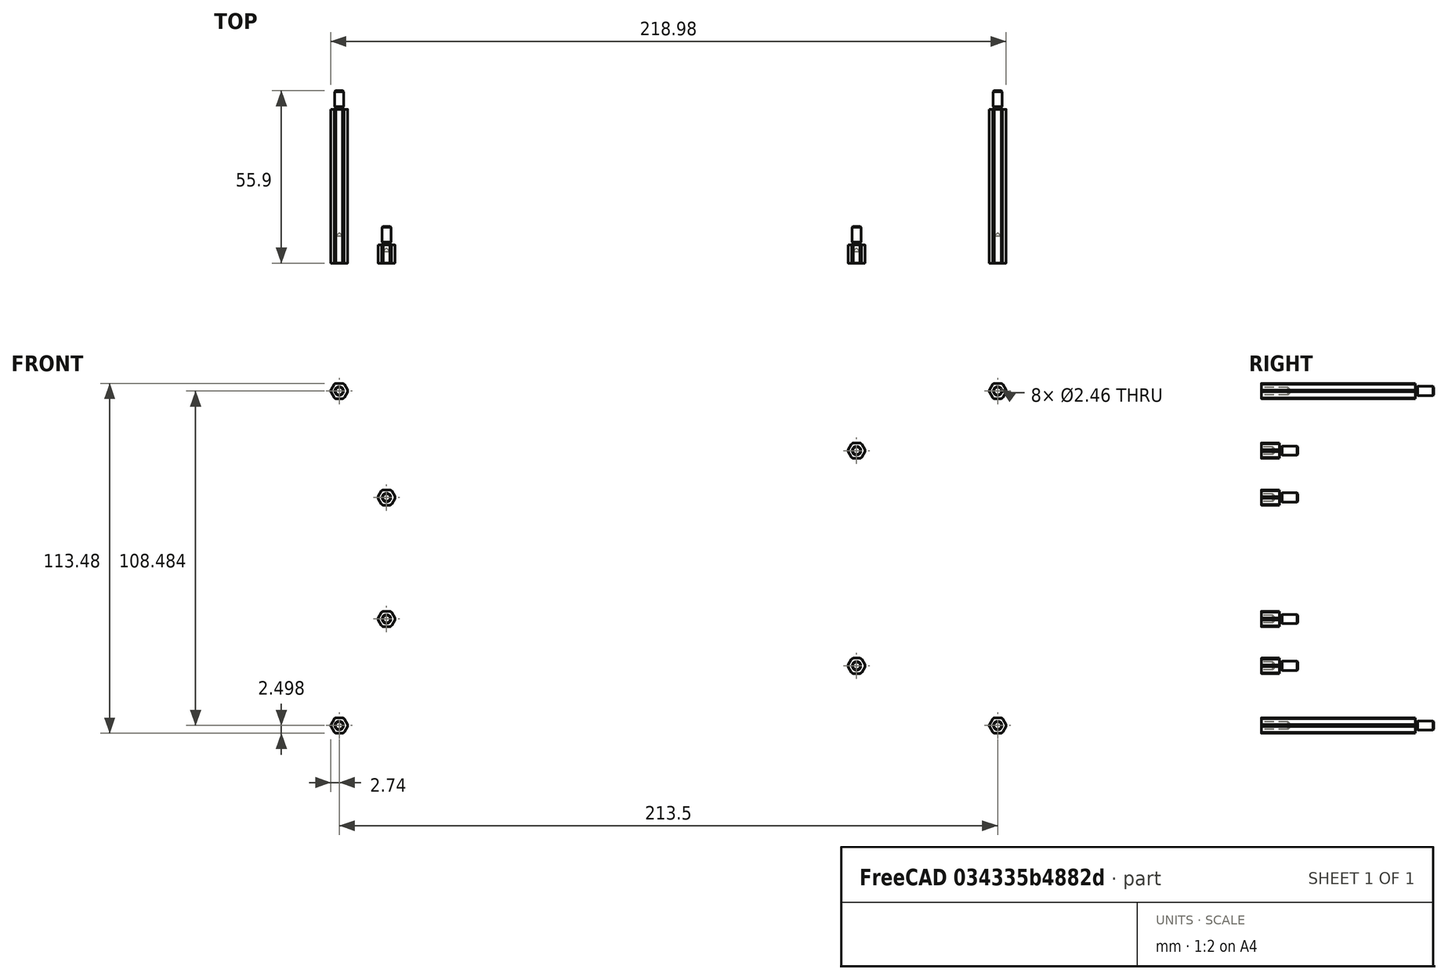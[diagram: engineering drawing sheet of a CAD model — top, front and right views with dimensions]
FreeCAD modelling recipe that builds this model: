
FCSTD DOCUMENT  (FreeCAD 1.0R38641 +468 (Git))
Label: psu
License: All rights reserved
LicenseURL: https://en.wikipedia.org/wiki/All_rights_reserved
objects: App::Link×8, App::FeaturePython×8, Part::FeaturePython×8, Assembly::JointGroup×1, Assembly::AssemblyObject×1
note: 8 computed .brp shape members not serialized (recipe doc carries the construction recipe); baked Part::Feature solids carry a one-line shape summary decoded from their .brp
EXTERNAL_REF file=parts/psu/psu_top_and_bottom.FCStd obj=Body
EXTERNAL_REF file=parts/psu/psu_side_short.FCStd obj=Body
EXTERNAL_REF file=parts/psu/psu_side_long.FCStd obj=Body
EXTERNAL_REF file=third_party/qualtek_power_entry.FCStd obj=Body
EXTERNAL_REF file=parts/dimensions.FCStd obj=VarSet
EXTERNAL_REF file=third_party/doepfer_psu3.FCStd obj=Body

FEATURE [App::Link] PsuTopAndBottom
  LinkedObject = -> <external parts/psu/psu_top_and_bottom.FCStd>#Body
FEATURE [App::FeaturePython] GroundedJoint  # Assembly grounded joint (typed FeaturePython)
  ObjectToGround = -> PsuTopAndBottom
FEATURE [App::Link] PsuTopAndBottom001
  LinkPlacement = pos=(-6e-15,-51.8542,-3e-16) rot=(0,0,1;0rad)
  LinkedObject = -> <external parts/psu/psu_top_and_bottom.FCStd>#Body
  Placement = pos=(-6e-15,-51.8542,-3e-16) rot=(0,0,1;0rad)
FEATURE [App::Link] PsuSideShort
  LinkPlacement = pos=(0.127,-51.8542,1.5e-14) rot=(0,0,1;0rad)
  LinkedObject = -> <external parts/psu/psu_side_short.FCStd>#Body
  Placement = pos=(0.127,-51.8542,1.5e-14) rot=(0,0,1;0rad)
FEATURE [App::Link] PsuSideShort001
  LinkPlacement = pos=(-227.198,-51.8542,1.832e-13) rot=(0,0,1;0rad)
  LinkedObject = -> <external parts/psu/psu_side_short.FCStd>#Body
  Placement = pos=(-227.198,-51.8542,1.832e-13) rot=(0,0,1;0rad)
FEATURE [App::Link] PsuSideLong
  LinkPlacement = pos=(2.22e-14,-51.8542,0.127) rot=(0,0,1;0rad)
  LinkedObject = -> <external parts/psu/psu_side_long.FCStd>#Body
  Placement = pos=(2.22e-14,-51.8542,0.127) rot=(0,0,1;0rad)
FEATURE [App::Link] PsuSideLong001
  LinkPlacement = pos=(2.26e-14,-51.8542,-86.1976) rot=(0,0,1;0rad)
  LinkedObject = -> <external parts/psu/psu_side_long.FCStd>#Body
  Placement = pos=(2.26e-14,-51.8542,-86.1976) rot=(0,0,1;0rad)
FEATURE [App::Link] PowerEntry
  LinkPlacement = pos=(333.089,127.227,-56.25) rot=(0,0.707107,-0.707107;3.14159rad)
  LinkedObject = -> <external third_party/qualtek_power_entry.FCStd>#Body
  Placement = pos=(333.089,127.227,-56.25) rot=(0,0.707107,-0.707107;3.14159rad)
FEATURE [App::FeaturePython] Joint  label="Fixed"  # Assembly joint (typed FeaturePython)
  Activated = true
  AngleMax = 0
  AngleMin = 0
  Detach1 = false
  Detach2 = false
  Distance = 0
  Distance2 = 0
  EnableAngleMax = false
  EnableAngleMin = false
  EnableLengthMax = false
  EnableLengthMin = false
  JointType = 0 (Fixed)
  LengthMax = 0
  LengthMin = 0
  Offset2 = pos=(0.127,0,0.127) rot=(0,0,1;0rad)
  Placement1 = pos=(328.216,127.227,-24.579) rot=(0,0,1;0rad)
  Placement2 = pos=(328.089,179.081,-24.579) rot=(0,0,1;0rad)
  Reference1 = -> Assembly [PsuTopAndBottom.Vertex91,PsuTopAndBottom.Vertex91]
  Reference2 = -> Assembly [PsuSideShort.Vertex42,PsuSideShort.Vertex42]
  expr: .Offset2.Base.x = dimensions#VarSet.EnclosureFinishThickness
  expr: .Offset2.Base.z = dimensions#VarSet.EnclosureFinishThickness
FEATURE [App::FeaturePython] Joint001  label="Fixed001"  # Assembly joint (typed FeaturePython)
  Activated = true
  AngleMax = 0
  AngleMin = 0
  Detach1 = false
  Detach2 = false
  Distance = 0
  Distance2 = 0
  EnableAngleMax = false
  EnableAngleMin = false
  EnableLengthMax = false
  EnableLengthMin = false
  JointType = 0 (Fixed)
  LengthMax = 0
  LengthMin = 0
  Offset1 = pos=(0.127,0,0.127) rot=(0,0,1;0rad)
  Placement1 = pos=(328.089,179.081,-24.579) rot=(0,0,1;0rad)
  Placement2 = pos=(100.892,127.227,-24.579) rot=(0,0,1;0rad)
  Reference1 = -> Assembly [PsuSideShort001.Vertex42,PsuSideShort001.Vertex42]
  Reference2 = -> Assembly [PsuTopAndBottom.Vertex67,PsuTopAndBottom.Vertex67]
  expr: .Offset1.Base.x = dimensions#VarSet.EnclosureFinishThickness
  expr: .Offset1.Base.z = dimensions#VarSet.EnclosureFinishThickness
FEATURE [App::FeaturePython] Joint002  label="Fixed002"  # Assembly joint (typed FeaturePython)
  Activated = true
  AngleMax = 0
  AngleMin = 0
  Detach1 = false
  Detach2 = false
  Distance = 0
  Distance2 = 0
  EnableAngleMax = false
  EnableAngleMin = false
  EnableLengthMax = false
  EnableLengthMin = false
  JointType = 0 (Fixed)
  LengthMax = 0
  LengthMin = 0
  Offset2 = pos=(0.127,0,0.127) rot=(0,0,1;0rad)
  Placement1 = pos=(328.216,127.227,-24.579) rot=(0,0,1;0rad)
  Placement2 = pos=(328.089,127.227,-24.579) rot=(0,0,1;0rad)
  Reference1 = -> Assembly [PsuTopAndBottom001.Vertex91,PsuTopAndBottom001.Vertex91]
  Reference2 = -> Assembly [PsuSideShort.Vertex10,PsuSideShort.Vertex10]
  expr: .Offset2.Base.x = dimensions#VarSet.EnclosureFinishThickness
  expr: .Offset2.Base.z = dimensions#VarSet.EnclosureFinishThickness
FEATURE [App::FeaturePython] Joint003  label="Fixed003"  # Assembly joint (typed FeaturePython)
  Activated = true
  AngleMax = 0
  AngleMin = 0
  Detach1 = false
  Detach2 = false
  Distance = 0
  Distance2 = 0
  EnableAngleMax = false
  EnableAngleMin = false
  EnableLengthMax = false
  EnableLengthMin = false
  JointType = 0 (Fixed)
  LengthMax = 0
  LengthMin = 0
  Offset1 = pos=(0.127,0,0.127) rot=(0,0,1;0rad)
  Placement1 = pos=(303.647,127.227,-12.1606) rot=(0,0,1;0rad)
  Placement2 = pos=(303.647,127.227,-12.0336) rot=(0,0,1;0rad)
  Reference1 = -> Assembly [PsuSideLong.Vertex28,PsuSideLong.Vertex28]
  Reference2 = -> Assembly [PsuTopAndBottom001.Vertex105,PsuTopAndBottom001.Vertex105]
  expr: .Offset1.Base.x = dimensions#VarSet.EnclosureFinishThickness
  expr: .Offset1.Base.z = dimensions#VarSet.EnclosureFinishThickness
FEATURE [App::FeaturePython] Joint004  label="Fixed004"  # Assembly joint (typed FeaturePython)
  Activated = true
  AngleMax = 0
  AngleMin = 0
  Detach1 = false
  Detach2 = false
  Distance = 0
  Distance2 = 0
  EnableAngleMax = false
  EnableAngleMin = false
  EnableLengthMax = false
  EnableLengthMin = false
  JointType = 0 (Fixed)
  LengthMax = 0
  LengthMin = 0
  Offset1 = pos=(-0.127,0,-0.127) rot=(0,0,1;0rad)
  Placement1 = pos=(303.52,127.227,-98.4852) rot=(0,0,1;0rad)
  Placement2 = pos=(303.52,127.227,-12.2876) rot=(0,0,1;0rad)
  Reference1 = -> Assembly [PsuTopAndBottom001.Vertex97,PsuTopAndBottom001.Vertex97]
  Reference2 = -> Assembly [PsuSideLong001.Vertex28,PsuSideLong001.Vertex28]
  expr: .Offset1.Base.x = -dimensions#VarSet.EnclosureFinishThickness
  expr: .Offset1.Base.z = -dimensions#VarSet.EnclosureFinishThickness
FEATURE [App::FeaturePython] Joint007  label="Fixed007"  # Assembly joint (typed FeaturePython)
  Activated = true
  AngleMax = 0
  AngleMin = 0
  Detach1 = false
  Detach2 = false
  Distance = 0
  Distance2 = 0
  EnableAngleMax = false
  EnableAngleMin = false
  EnableLengthMax = false
  EnableLengthMin = false
  JointType = 0 (Fixed)
  LengthMax = 0
  LengthMin = 0
  Offset2 = pos=(0,0,0) rot=(0,0,-1;1.5708rad)
  Placement1 = pos=(5,-7.1e-15,5) rot=(-0.57735,-0.57735,0.57735;2.0944rad)
  Placement2 = pos=(327.962,174.081,-56.25) rot=(0,1,0;1.5708rad)
  Reference1 = -> Assembly [PowerEntry.Edge36,PowerEntry.Edge36]
  Reference2 = -> Assembly [PsuSideShort.Edge123,PsuSideShort.Edge123]
FEATURE [Part::FeaturePython] Standoff  label="M3x6x5-Standoff"  # WARN: FeaturePython — macro-defined, semantics opaque (R4)
  BaseObject = -> PsuTopAndBottom001 [Pad.Edge183]
  Diameter = 2
  Invert = true
  LeftHanded = false
  Length = 4
  LengthCustom = 6
  MatchOuter = false
  Offset = -6
  OffsetAngle = 0
  Placement = pos=(274.5,83.2271,-21.35) rot=(1,0,0;1.5708rad)
  ScrewLength = 6
  Thread = false
  Type = 0
  Width = 0
FEATURE [Part::FeaturePython] Standoff001  label="M3x6x5-Standoff019"  # WARN: FeaturePython — macro-defined, semantics opaque (R4)
  BaseObject = -> PsuTopAndBottom001 [Pad.Edge186]
  Diameter = 2
  Invert = true
  LeftHanded = false
  Length = 4
  LengthCustom = 6
  MatchOuter = false
  Offset = -6
  OffsetAngle = 0
  Placement = pos=(122.1,83.2271,-36.55) rot=(1,0,0;1.5708rad)
  ScrewLength = 6
  Thread = false
  Type = 0
  Width = 0
FEATURE [Part::FeaturePython] Standoff002  label="M3x6x5-Standoff020"  # WARN: FeaturePython — macro-defined, semantics opaque (R4)
  BaseObject = -> PsuTopAndBottom001 [Pad.Edge192]
  Diameter = 2
  Invert = true
  LeftHanded = false
  Length = 4
  LengthCustom = 6
  MatchOuter = false
  Offset = -6
  OffsetAngle = 0
  Placement = pos=(122.1,83.2271,-75.95) rot=(1,0,0;1.5708rad)
  ScrewLength = 6
  Thread = false
  Type = 0
  Width = 0
FEATURE [Part::FeaturePython] Standoff003  label="M3x6x5-Standoff021"  # WARN: FeaturePython — macro-defined, semantics opaque (R4)
  BaseObject = -> PsuTopAndBottom001 [Pad.Edge189]
  Diameter = 2
  Invert = true
  LeftHanded = false
  Length = 4
  LengthCustom = 6
  MatchOuter = false
  Offset = -6
  OffsetAngle = 0
  Placement = pos=(274.5,83.2271,-91.15) rot=(1,0,0;1.5708rad)
  ScrewLength = 6
  Thread = false
  Type = 0
  Width = 0
FEATURE [App::Link] Psu
  LinkPlacement = pos=(103,83.2271,-16.25) rot=(-1,0,0;1.5708rad)
  LinkedObject = -> <external third_party/doepfer_psu3.FCStd>#Body
  Placement = pos=(103,83.2271,-16.25) rot=(-1,0,0;1.5708rad)
FEATURE [App::FeaturePython] Joint008  label="Fixed008"  # Assembly joint (typed FeaturePython)
  Activated = true
  AngleMax = 0
  AngleMin = 0
  Detach1 = false
  Detach2 = false
  Distance = 0
  Distance2 = 0
  EnableAngleMax = false
  EnableAngleMin = false
  EnableLengthMax = false
  EnableLengthMin = false
  JointType = 0 (Fixed)
  LengthMax = 0
  LengthMin = 0
  Offset1 = pos=(0,0,-6) rot=(0,-1,0;3.14159rad)
  Placement1 = pos=(19.1,20.3,-6) rot=(0,-1,0;3.14159rad)
  Placement2 = pos=(122.1,129.081,-36.55) rot=(0,0.707107,0.707107;3.14159rad)
  Reference1 = -> Assembly [Psu.Edge20,Psu.Edge20]
  Reference2 = -> Assembly [PsuTopAndBottom001.Edge186,PsuTopAndBottom001.Edge186]
FEATURE [Assembly::JointGroup] Joints
  Group = -> [GroundedJoint,Joint,Joint001,Joint002,Joint003,Joint004,Joint007,Joint008]
FEATURE [Part::FeaturePython] Standoff004  label="M3x50x5-Standoff"  # WARN: FeaturePython — macro-defined, semantics opaque (R4)
  BaseObject = -> PsuTopAndBottom001 [Pad.Edge174]
  Diameter = 2
  Invert = true
  LeftHanded = false
  Length = 4
  LengthCustom = 50
  MatchOuter = false
  Offset = -50
  OffsetAngle = 0
  Placement = pos=(320.25,127.227,-2.0081) rot=(1,0,0;1.5708rad)
  ScrewLength = 6
  Thread = false
  Type = 0
  Width = 0
FEATURE [Part::FeaturePython] Standoff005  label="M3x50x5-Standoff007"  # WARN: FeaturePython — macro-defined, semantics opaque (R4)
  BaseObject = -> PsuTopAndBottom001 [Pad.Edge180]
  Diameter = 2
  Invert = true
  LeftHanded = false
  Length = 4
  LengthCustom = 50
  MatchOuter = false
  Offset = -50
  OffsetAngle = 0
  Placement = pos=(106.75,127.227,-2.0081) rot=(1,0,0;1.5708rad)
  ScrewLength = 6
  Thread = false
  Type = 0
  Width = 0
FEATURE [Part::FeaturePython] Standoff006  label="M3x50x5-Standoff008"  # WARN: FeaturePython — macro-defined, semantics opaque (R4)
  BaseObject = -> PsuTopAndBottom001 [Pad.Edge171]
  Diameter = 2
  Invert = true
  LeftHanded = false
  Length = 4
  LengthCustom = 50
  MatchOuter = false
  Offset = -50
  OffsetAngle = 0
  Placement = pos=(320.25,127.227,-110.492) rot=(1,0,0;1.5708rad)
  ScrewLength = 6
  Thread = false
  Type = 0
  Width = 0
FEATURE [Part::FeaturePython] Standoff007  label="M3x50x5-Standoff009"  # WARN: FeaturePython — macro-defined, semantics opaque (R4)
  BaseObject = -> PsuTopAndBottom001 [Pad.Edge177]
  Diameter = 2
  Invert = true
  LeftHanded = false
  Length = 4
  LengthCustom = 50
  MatchOuter = false
  Offset = -50
  OffsetAngle = 0
  Placement = pos=(106.75,127.227,-110.492) rot=(1,0,0;1.5708rad)
  ScrewLength = 6
  Thread = false
  Type = 0
  Width = 0
FEATURE [Assembly::AssemblyObject] Assembly  label="PsuAssembly"
  Group = -> [Joints,PsuTopAndBottom,GroundedJoint,PsuTopAndBottom001,PsuSideShort,PsuSideShort001,PsuSideLong,PsuSideLong001,PowerEntry,Joint,Joint001,Joint002,Joint003,Joint004,Joint007,Psu,Joint008,Standoff,Standoff001,Standoff002,Standoff003,Standoff004,Standoff005,Standoff006,Standoff007]
  Origin = -> Origin
  Type = Assembly

RESOLVED EXTERNAL PARTS (link-assembly join: the EXTERNAL_REF files above that resolve inside this repo's crawl, each included once):
---- part parts/psu/psu_side_long.FCStd = doc fcstd_292d7ca47439 ----
FCSTD DOCUMENT  (FreeCAD 1.0R38641 +468 (Git))
Label: psu_side_long
License: All rights reserved
LicenseURL: https://en.wikipedia.org/wiki/All_rights_reserved
objects: PartDesign::SubShapeBinder×2, Sketcher::SketchObject×1, PartDesign::Pad×1, PartDesign::Body×1
note: 8 computed .brp shape members not serialized (recipe doc carries the construction recipe); baked Part::Feature solids carry a one-line shape summary decoded from their .brp
EXTERNAL_REF file=../dimensions.FCStd obj=VarSet
EXTERNAL_REF file=psu_side_short.FCStd obj=Body
EXTERNAL_REF file=psu_top_and_bottom.FCStd obj=Body

FEATURE [PartDesign::SubShapeBinder] Binder  label="PsuSideShortBinderBinder"
  BindCopyOnChange = 0
  BindMode = 0
  ClaimChildren = false
  Context = -> Body [Binder.]
  Fuse = false
  MakeFace = true
  OffsetFill = false
  OffsetIntersection = false
  OffsetJoinType = 0
  OffsetOpenResult = false
  PartialLoad = false
  Placement = pos=(0.127,0,0) rot=(0,0,1;0rad)
  Refine = true
  Relative = true
  Support = -> [<external psu_side_short.FCStd>#Body]
  _Version = 2
  expr: .Placement.Base.x = dimensions#VarSet.EnclosureFinishThickness
FEATURE [PartDesign::SubShapeBinder] Binder001  label="PsuTopAndBottomBinder"
  BindCopyOnChange = 0
  BindMode = 0
  ClaimChildren = false
  Context = -> Body [Binder001.]
  Fuse = false
  MakeFace = true
  OffsetFill = false
  OffsetIntersection = false
  OffsetJoinType = 0
  OffsetOpenResult = false
  PartialLoad = false
  Refine = true
  Relative = true
  Support = -> [<external psu_top_and_bottom.FCStd>#Body]
  _Version = 2
FEATURE [Sketcher::SketchObject] Sketch
  ArcFitTolerance = 1e-06
  AttachmentSupport = -> [Binder001]
  ExternalGeometry = -> [Binder001,Binder]
  FullyConstrained = true
  MakeInternals = false
  MapMode = 5
  Placement = pos=(0,-3.1e-15,-14.1418) rot=(0,0,1;0rad)
  expr: Constraints[183] = dimensions#VarSet.EnclosureCornerRadius
  expr: Constraints[49] = dimensions#VarSet.EnclosureFinishThickness
  sketch-geometry (113):
    g0: LineSegment [constr] StartX=303.647 StartY=129.081 StartZ=0 EndX=303.52 EndY=129.081 EndZ=0
    g1: LineSegment [constr] StartX=240.305 StartY=129.081 StartZ=0 EndX=240.178 EndY=129.081 EndZ=0
    g2: LineSegment [constr] StartX=123.353 StartY=129.081 StartZ=0 EndX=123.48 EndY=129.081 EndZ=0
    g3: LineSegment [constr] StartX=186.695 StartY=129.081 StartZ=0 EndX=186.568 EndY=129.081 EndZ=0
    g4: LineSegment [constr] StartX=326.235 StartY=133.444 StartZ=0 EndX=326.235 EndY=133.571 EndZ=0
    g5: LineSegment [constr] StartX=326.235 StartY=174.719 StartZ=0 EndX=326.235 EndY=174.592 EndZ=0
    g6: LineSegment StartX=326.235 StartY=174.592 StartZ=0 EndX=328.089 EndY=174.592 EndZ=0
    g7: LineSegment StartX=329.289 StartY=173.392 StartZ=0 EndX=329.289 EndY=134.771 EndZ=0
    g8: LineSegment StartX=328.089 StartY=133.571 StartZ=0 EndX=326.235 EndY=133.571 EndZ=0
    g9: LineSegment StartX=303.52 StartY=129.081 StartZ=0 EndX=303.52 EndY=127.227 EndZ=0
    g10: LineSegment StartX=240.178 StartY=129.081 StartZ=0 EndX=240.178 EndY=127.227 EndZ=0
    g11: LineSegment StartX=241.378 StartY=126.027 StartZ=0 EndX=302.32 EndY=126.027 EndZ=0
    g12: LineSegment StartX=186.568 StartY=129.081 StartZ=0 EndX=186.568 EndY=127.227 EndZ=0
    g13: LineSegment StartX=123.48 StartY=129.081 StartZ=0 EndX=123.48 EndY=127.227 EndZ=0
    g14: LineSegment StartX=124.68 StartY=126.027 StartZ=0 EndX=185.368 EndY=126.027 EndZ=0
    g15: LineSegment StartX=240.178 StartY=179.081 StartZ=0 EndX=240.178 EndY=180.935 EndZ=0
    g16: LineSegment StartX=241.378 StartY=182.135 StartZ=0 EndX=302.32 EndY=182.135 EndZ=0
    g17: LineSegment StartX=303.52 StartY=180.935 StartZ=0 EndX=303.52 EndY=179.081 EndZ=0
    g18: LineSegment StartX=304.72 StartY=130.281 StartZ=0 EndX=323.835 EndY=130.281 EndZ=0
    g19: LineSegment StartX=325.035 StartY=131.481 StartZ=0 EndX=325.035 EndY=132.371 EndZ=0
    g20: LineSegment StartX=304.72 StartY=177.881 StartZ=0 EndX=323.835 EndY=177.881 EndZ=0
    g21: LineSegment StartX=325.035 StartY=176.681 StartZ=0 EndX=325.035 EndY=175.792 EndZ=0
    g22: LineSegment StartX=187.768 StartY=130.281 StartZ=0 EndX=238.978 EndY=130.281 EndZ=0
    g23: LineSegment StartX=122.28 StartY=130.281 StartZ=0 EndX=103.165 EndY=130.281 EndZ=0
    g24: LineSegment StartX=101.965 StartY=131.481 StartZ=0 EndX=101.965 EndY=132.371 EndZ=0
    g25: LineSegment StartX=100.765 StartY=133.571 StartZ=0 EndX=98.9106 EndY=133.571 EndZ=0
    g26: LineSegment StartX=97.7106 StartY=134.771 StartZ=0 EndX=97.7106 EndY=173.392 EndZ=0
    g27: LineSegment StartX=98.9106 StartY=174.592 StartZ=0 EndX=100.765 EndY=174.592 EndZ=0
    g28: LineSegment StartX=101.965 StartY=175.792 StartZ=0 EndX=101.965 EndY=176.681 EndZ=0
    g29: LineSegment StartX=103.165 StartY=177.881 StartZ=0 EndX=122.28 EndY=177.881 EndZ=0
    g30: LineSegment StartX=123.48 StartY=179.081 StartZ=0 EndX=123.48 EndY=180.935 EndZ=0
    g31: LineSegment StartX=124.68 StartY=182.135 StartZ=0 EndX=185.368 EndY=182.135 EndZ=0
    g32: LineSegment StartX=186.568 StartY=180.935 StartZ=0 EndX=186.568 EndY=179.081 EndZ=0
    g33: LineSegment StartX=238.978 StartY=177.881 StartZ=0 EndX=187.768 EndY=177.881 EndZ=0
    g34: ArcOfCircle CenterX=122.28 CenterY=129.081 CenterZ=0 NormalX=0 NormalY=0 NormalZ=1 AngleXU=0 Radius=1.2 StartAngle=4.2e-15 EndAngle=1.5708
    g35: ArcOfCircle CenterX=187.768 CenterY=129.081 CenterZ=0 NormalX=0 NormalY=0 NormalZ=1 AngleXU=0 Radius=1.2 StartAngle=1.5708 EndAngle=3.14159
    g36: ArcOfCircle CenterX=238.978 CenterY=129.081 CenterZ=0 NormalX=0 NormalY=0 NormalZ=1 AngleXU=0 Radius=1.2 StartAngle=2.7e-15 EndAngle=1.5708
    g37: ArcOfCircle CenterX=304.72 CenterY=129.081 CenterZ=0 NormalX=0 NormalY=0 NormalZ=1 AngleXU=0 Radius=1.2 StartAngle=1.5708 EndAngle=3.14159
    g38: ArcOfCircle CenterX=326.235 CenterY=132.371 CenterZ=0 NormalX=0 NormalY=0 NormalZ=1 AngleXU=0 Radius=1.2 StartAngle=1.5708 EndAngle=3.14159
    g39: ArcOfCircle CenterX=326.235 CenterY=175.792 CenterZ=0 NormalX=0 NormalY=0 NormalZ=1 AngleXU=0 Radius=1.2 StartAngle=3.14159 EndAngle=4.71239
    g40: ArcOfCircle CenterX=328.089 CenterY=134.771 CenterZ=0 NormalX=0 NormalY=0 NormalZ=1 AngleXU=0 Radius=1.2 StartAngle=4.71239 EndAngle=6.28319
    g41: GeomPoint [constr] X=329.289 Y=133.571 Z=0
    g42: ArcOfCircle CenterX=328.089 CenterY=173.392 CenterZ=0 NormalX=0 NormalY=0 NormalZ=1 AngleXU=0 Radius=1.2 StartAngle=1.01e-14 EndAngle=1.5708
    g43: GeomPoint [constr] X=329.289 Y=174.592 Z=0
    g44: ArcOfCircle CenterX=323.835 CenterY=176.681 CenterZ=0 NormalX=0 NormalY=0 NormalZ=1 AngleXU=0 Radius=1.2 StartAngle=1.12e-14 EndAngle=1.5708
    g45: GeomPoint [constr] X=325.035 Y=177.881 Z=0
    g46: ArcOfCircle CenterX=304.72 CenterY=179.081 CenterZ=0 NormalX=0 NormalY=0 NormalZ=1 AngleXU=0 Radius=1.2 StartAngle=3.14159 EndAngle=4.71239
    g47: GeomPoint [constr] X=303.52 Y=177.881 Z=0
    g48: ArcOfCircle CenterX=302.32 CenterY=180.935 CenterZ=0 NormalX=0 NormalY=0 NormalZ=1 AngleXU=0 Radius=1.2 StartAngle=6.9e-15 EndAngle=1.5708
    g49: GeomPoint [constr] X=303.52 Y=182.135 Z=0
    g50: ArcOfCircle CenterX=241.378 CenterY=180.935 CenterZ=0 NormalX=0 NormalY=0 NormalZ=1 AngleXU=0 Radius=1.2 StartAngle=1.5708 EndAngle=3.14159
    g51: GeomPoint [constr] X=240.178 Y=182.135 Z=0
    g52: ArcOfCircle CenterX=238.978 CenterY=179.081 CenterZ=0 NormalX=0 NormalY=0 NormalZ=1 AngleXU=0 Radius=1.2 StartAngle=4.71239 EndAngle=6.28319
    g53: GeomPoint [constr] X=240.178 Y=177.881 Z=0
    g54: ArcOfCircle CenterX=187.768 CenterY=179.081 CenterZ=0 NormalX=0 NormalY=0 NormalZ=1 AngleXU=0 Radius=1.2 StartAngle=3.14159 EndAngle=4.71239
    g55: GeomPoint [constr] X=186.568 Y=177.881 Z=0
    g56: ArcOfCircle CenterX=185.368 CenterY=180.935 CenterZ=0 NormalX=0 NormalY=0 NormalZ=1 AngleXU=0 Radius=1.2 StartAngle=-1.07e-14 EndAngle=1.5708
    g57: GeomPoint [constr] X=186.568 Y=182.135 Z=0
    g58: ArcOfCircle CenterX=124.68 CenterY=180.935 CenterZ=0 NormalX=0 NormalY=0 NormalZ=1 AngleXU=0 Radius=1.2 StartAngle=1.5708 EndAngle=3.14159
    g59: GeomPoint [constr] X=123.48 Y=182.135 Z=0
    g60: ArcOfCircle CenterX=122.28 CenterY=179.081 CenterZ=0 NormalX=0 NormalY=0 NormalZ=1 AngleXU=0 Radius=1.2 StartAngle=4.71239 EndAngle=6.28319
    g61: GeomPoint [constr] X=123.48 Y=177.881 Z=0
    g62: ArcOfCircle CenterX=103.165 CenterY=176.681 CenterZ=0 NormalX=0 NormalY=0 NormalZ=1 AngleXU=0 Radius=1.2 StartAngle=1.5708 EndAngle=3.14159
    g63: GeomPoint [constr] X=101.965 Y=177.881 Z=0
    g64: ArcOfCircle CenterX=100.765 CenterY=175.792 CenterZ=0 NormalX=0 NormalY=0 NormalZ=1 AngleXU=0 Radius=1.2 StartAngle=4.71239 EndAngle=6.28319
    g65: GeomPoint [constr] X=101.965 Y=174.592 Z=0
    g66: ArcOfCircle CenterX=98.9106 CenterY=173.392 CenterZ=0 NormalX=0 NormalY=0 NormalZ=1 AngleXU=0 Radius=1.2 StartAngle=1.5708 EndAngle=3.14159
    g67: GeomPoint [constr] X=97.7106 Y=174.592 Z=0
    g68: ArcOfCircle CenterX=98.9106 CenterY=134.771 CenterZ=0 NormalX=0 NormalY=0 NormalZ=1 AngleXU=0 Radius=1.2 StartAngle=3.14159 EndAngle=4.71239
    g69: GeomPoint [constr] X=97.7106 Y=133.571 Z=0
    g70: ArcOfCircle CenterX=100.765 CenterY=132.371 CenterZ=0 NormalX=0 NormalY=0 NormalZ=1 AngleXU=0 Radius=1.2 StartAngle=-8e-15 EndAngle=1.5708
    g71: GeomPoint [constr] X=101.965 Y=133.571 Z=0
    g72: ArcOfCircle CenterX=103.165 CenterY=131.481 CenterZ=0 NormalX=0 NormalY=0 NormalZ=1 AngleXU=0 Radius=1.2 StartAngle=3.14159 EndAngle=4.71239
    g73: GeomPoint [constr] X=101.965 Y=130.281 Z=0
    g74: ArcOfCircle CenterX=124.68 CenterY=127.227 CenterZ=0 NormalX=0 NormalY=0 NormalZ=1 AngleXU=0 Radius=1.2 StartAngle=3.14159 EndAngle=4.71239
    g75: GeomPoint [constr] X=123.48 Y=126.027 Z=0
    g76: ArcOfCircle CenterX=185.368 CenterY=127.227 CenterZ=0 NormalX=0 NormalY=0 NormalZ=1 AngleXU=0 Radius=1.2 StartAngle=4.71239 EndAngle=6.28319
    g77: GeomPoint [constr] X=186.568 Y=126.027 Z=0
    g78: ArcOfCircle CenterX=241.378 CenterY=127.227 CenterZ=0 NormalX=0 NormalY=0 NormalZ=1 AngleXU=0 Radius=1.2 StartAngle=3.14159 EndAngle=4.71239
    g79: GeomPoint [constr] X=240.178 Y=126.027 Z=0
    g80: ArcOfCircle CenterX=302.32 CenterY=127.227 CenterZ=0 NormalX=0 NormalY=0 NormalZ=1 AngleXU=0 Radius=1.2 StartAngle=4.71239 EndAngle=6.28319
    g81: GeomPoint [constr] X=303.52 Y=126.027 Z=0
    g82: ArcOfCircle CenterX=323.835 CenterY=131.481 CenterZ=0 NormalX=0 NormalY=0 NormalZ=1 AngleXU=0 Radius=1.2 StartAngle=4.71239 EndAngle=6.28319
    g83: GeomPoint [constr] X=325.035 Y=130.281 Z=0
    g84: LineSegment [constr] StartX=120.6 StartY=129.081 StartZ=0 EndX=120.6 EndY=126.027 EndZ=0
    g85: LineSegment [constr] StartX=120.6 StartY=126.027 StartZ=0 EndX=124.68 EndY=126.027 EndZ=0
    g86: LineSegment [constr] StartX=185.368 StartY=126.027 StartZ=0 EndX=189.448 EndY=126.027 EndZ=0
    g87: LineSegment [constr] StartX=189.448 StartY=126.027 StartZ=0 EndX=189.448 EndY=139.081 EndZ=0
    g88: LineSegment [constr] StartX=120.6 StartY=129.081 StartZ=0 EndX=120.6 EndY=139.081 EndZ=0
    g89: ArcOfCircle CenterX=120.6 CenterY=141.224 CenterZ=0 NormalX=0 NormalY=0 NormalZ=1 AngleXU=0 Radius=2.14286 StartAngle=1.5708 EndAngle=4.71239
    g90: ArcOfCircle CenterX=189.448 CenterY=141.224 CenterZ=0 NormalX=0 NormalY=0 NormalZ=1 AngleXU=0 Radius=2.14286 StartAngle=4.71239 EndAngle=7.85398
    g91: LineSegment StartX=120.6 StartY=143.367 StartZ=0 EndX=189.448 EndY=143.367 EndZ=0
    g92: LineSegment StartX=120.6 StartY=139.081 StartZ=0 EndX=189.448 EndY=139.081 EndZ=0
    g93: ArcOfCircle CenterX=120.6 CenterY=149.796 CenterZ=0 NormalX=0 NormalY=0 NormalZ=1 AngleXU=0 Radius=2.14286 StartAngle=1.5708 EndAngle=4.71239
    g94: ArcOfCircle CenterX=189.448 CenterY=149.796 CenterZ=0 NormalX=0 NormalY=0 NormalZ=1 AngleXU=0 Radius=2.14286 StartAngle=4.71239 EndAngle=7.85398
    g95: LineSegment StartX=120.6 StartY=151.938 StartZ=0 EndX=189.448 EndY=151.938 EndZ=0
    g96: LineSegment StartX=120.6 StartY=147.653 StartZ=0 EndX=189.448 EndY=147.653 EndZ=0
    g97: LineSegment [constr] StartX=120.6 StartY=139.081 StartZ=0 EndX=120.6 EndY=143.367 EndZ=0
    g98: LineSegment [constr] StartX=120.6 StartY=143.367 StartZ=0 EndX=120.6 EndY=147.653 EndZ=0
    g99: LineSegment [constr] StartX=120.6 StartY=147.653 StartZ=0 EndX=120.6 EndY=151.938 EndZ=0
    g100: LineSegment [constr] StartX=120.6 StartY=151.938 StartZ=0 EndX=120.6 EndY=156.224 EndZ=0
    g101: LineSegment [constr] StartX=120.6 StartY=156.224 StartZ=0 EndX=120.6 EndY=160.51 EndZ=0
    g102: LineSegment [constr] StartX=120.6 StartY=160.51 StartZ=0 EndX=120.6 EndY=164.796 EndZ=0
    g103: LineSegment [constr] StartX=120.6 StartY=164.796 StartZ=0 EndX=120.6 EndY=169.081 EndZ=0
    g104: ArcOfCircle CenterX=120.6 CenterY=158.367 CenterZ=0 NormalX=0 NormalY=0 NormalZ=1 AngleXU=0 Radius=2.14286 StartAngle=1.5708 EndAngle=4.71239
    g105: ArcOfCircle CenterX=189.448 CenterY=158.367 CenterZ=0 NormalX=0 NormalY=0 NormalZ=1 AngleXU=0 Radius=2.14286 StartAngle=4.71239 EndAngle=7.85398
    g106: LineSegment StartX=120.6 StartY=160.51 StartZ=0 EndX=189.448 EndY=160.51 EndZ=0
    g107: LineSegment StartX=120.6 StartY=156.224 StartZ=0 EndX=189.448 EndY=156.224 EndZ=0
    g108: ArcOfCircle CenterX=120.6 CenterY=166.938 CenterZ=0 NormalX=0 NormalY=0 NormalZ=1 AngleXU=0 Radius=2.14286 StartAngle=1.5708 EndAngle=4.71239
    g109: ArcOfCircle CenterX=189.448 CenterY=166.938 CenterZ=0 NormalX=0 NormalY=0 NormalZ=1 AngleXU=0 Radius=2.14286 StartAngle=4.71239 EndAngle=7.85398
    g110: LineSegment StartX=120.6 StartY=169.081 StartZ=0 EndX=189.448 EndY=169.081 EndZ=0
    g111: LineSegment StartX=120.6 StartY=164.796 StartZ=0 EndX=189.448 EndY=164.796 EndZ=0
    g112: LineSegment [constr] StartX=189.448 StartY=139.081 StartZ=0 EndX=189.448 EndY=169.081 EndZ=0
  constraints (266):
    c: Coincident(g0,g-4)
    c: PointOnObject(g0,g-4)
    c: Coincident(g1,g-4)
    c: Coincident(g2,g-3)
    c: Coincident(g3,g-3)
    c: Coincident(g4,g-5)
    c: PointOnObject(g4,g-5)
    c: Coincident(g5,g-5)
    c: PointOnObject(g5,g-5)
    c: Equal(g4,g5)
    c: Equal(g0,g4)
    c: Equal(g0,g1)
    c: Equal(g1,g3)
    c: Equal(g3,g2)
    c: Horizontal(g6)
    c: Vertical(g7)
    c: Horizontal(g8)
    c: Vertical(g9)
    c: Horizontal(g11)
    c: Vertical(g13)
    c: Horizontal(g14)
    c: Vertical(g15)
    c: Horizontal(g16)
    c: Vertical(g17)
    c: Horizontal(g18)
    c: Vertical(g19)
    c: Horizontal(g20)
    c: Vertical(g21)
    c: Horizontal(g23)
    c: Vertical(g24)
    c: Horizontal(g25)
    c: Vertical(g26)
    c: Horizontal(g27)
    c: Vertical(g28)
    c: Horizontal(g29)
    c: Vertical(g30)
    c: Horizontal(g31)
    c: Vertical(g32)
    c: Horizontal(g33)
    c: Tangent(g34,g23) = -1.5708
    c: Tangent(g37,g18) = 1.5708
    c: Tangent(g9,g37) = -1.5708
    c: Coincident(g9,g0)
    c: Tangent(g38,g8) = -1.5708
    c: Coincident(g8,g4)
    c: Tangent(g19,g38) = 1.5708
    c: Tangent(g6,g39) = -1.5708
    c: Coincident(g5,g6)
    c: Tangent(g39,g21) = -1.5708
    c: DistanceY(g4,g4) = 0.127
    c: PointOnObject(g41,g7)
    c: PointOnObject(g41,g8)
    c: Tangent(g7,g40) = 1.5708
    c: Tangent(g8,g40) = 1.5708
    c: PointOnObject(g43,g6)
    c: PointOnObject(g43,g7)
    c: Tangent(g6,g42) = 1.5708
    c: Tangent(g7,g42) = 1.5708
    c: PointOnObject(g45,g20)
    c: PointOnObject(g45,g21)
    c: Tangent(g20,g44) = 1.5708
    c: Tangent(g21,g44) = 1.5708
    c: PointOnObject(g47,g17)
    c: PointOnObject(g47,g20)
    c: Tangent(g17,g46) = -1.5708
    c: Tangent(g20,g46) = -1.5708
    c: PointOnObject(g49,g16)
    c: PointOnObject(g49,g17)
    c: Tangent(g16,g48) = 1.5708
    c: Tangent(g17,g48) = 1.5708
    c: PointOnObject(g51,g15)
    c: PointOnObject(g51,g16)
    c: Tangent(g15,g50) = 1.5708
    c: Tangent(g16,g50) = 1.5708
    c: PointOnObject(g53,g15)
    c: PointOnObject(g53,g33)
    c: Tangent(g15,g52) = -1.5708
    c: Tangent(g33,g52) = 1.5708
    c: PointOnObject(g55,g32)
    c: PointOnObject(g55,g33)
    c: Tangent(g32,g54) = -1.5708
    c: Tangent(g33,g54) = 1.5708
    c: PointOnObject(g57,g31)
    c: PointOnObject(g57,g32)
    c: Tangent(g31,g56) = 1.5708
    c: Tangent(g32,g56) = 1.5708
    c: PointOnObject(g59,g30)
    c: PointOnObject(g59,g31)
    c: Tangent(g30,g58) = 1.5708
    c: Tangent(g31,g58) = 1.5708
    c: PointOnObject(g61,g29)
    c: PointOnObject(g61,g30)
    c: Tangent(g29,g60) = -1.5708
    c: Tangent(g30,g60) = -1.5708
    c: PointOnObject(g63,g28)
    c: PointOnObject(g63,g29)
    c: Tangent(g28,g62) = 1.5708
    c: Tangent(g29,g62) = 1.5708
    c: PointOnObject(g65,g27)
    c: PointOnObject(g65,g28)
    c: Tangent(g27,g64) = -1.5708
    c: Tangent(g28,g64) = -1.5708
    c: PointOnObject(g67,g26)
    c: PointOnObject(g67,g27)
    c: Tangent(g26,g66) = 1.5708
    c: Tangent(g27,g66) = 1.5708
    c: PointOnObject(g69,g25)
    c: PointOnObject(g69,g26)
    c: Tangent(g25,g68) = 1.5708
    c: Tangent(g26,g68) = 1.5708
    c: PointOnObject(g71,g24)
    c: PointOnObject(g71,g25)
    c: Tangent(g24,g70) = -1.5708
    c: Tangent(g25,g70) = -1.5708
    c: PointOnObject(g73,g23)
    c: PointOnObject(g73,g24)
    c: Tangent(g23,g72) = 1.5708
    c: Tangent(g24,g72) = 1.5708
    c: PointOnObject(g75,g13)
    c: PointOnObject(g75,g14)
    c: Tangent(g13,g74) = -1.5708
    c: Tangent(g14,g74) = -1.5708
    c: PointOnObject(g77,g12)
    c: PointOnObject(g77,g14)
    c: Tangent(g12,g76) = 1.5708
    c: Tangent(g14,g76) = -1.5708
    c: PointOnObject(g79,g10)
    c: PointOnObject(g79,g11)
    c: Tangent(g10,g78) = -1.5708
    c: Tangent(g11,g78) = -1.5708
    c: PointOnObject(g81,g9)
    c: PointOnObject(g81,g11)
    c: Tangent(g9,g80) = 1.5708
    c: Tangent(g11,g80) = -1.5708
    c: PointOnObject(g83,g18)
    c: PointOnObject(g83,g19)
    c: Tangent(g18,g82) = -1.5708
    c: Tangent(g19,g82) = -1.5708
    c: Equal(g34,g35)
    c: Equal(g36,g37)
    c: Equal(g37,g38)
    c: Equal(g38,g39)
    c: Equal(g39,g40)
    c: Equal(g40,g42)
    c: Equal(g42,g44)
    c: Equal(g44,g46)
    c: Equal(g46,g48)
    c: Equal(g48,g50)
    c: Equal(g50,g52)
    c: Equal(g52,g54)
    c: Equal(g54,g56)
    c: Equal(g56,g58)
    c: Equal(g58,g60)
    c: Equal(g60,g62)
    c: Equal(g62,g64)
    c: Equal(g64,g66)
    c: Equal(g66,g68)
    c: Equal(g68,g70)
    c: Equal(g70,g72)
    c: Equal(g72,g74)
    c: Equal(g74,g76)
    c: Equal(g76,g78)
    c: Equal(g78,g80)
    c: Equal(g80,g82)
    c: Tangent(g35,g12) = -1.5708
    c: Tangent(g35,g22) = 1.5708
    c: Coincident(g12,g3)
    c: PointOnObject(g3,g-3)
    c: PointOnObject(g2,g-3)
    c: PointOnObject(g1,g-4)
    c: Tangent(g36,g10) = 1.5708
    c: Coincident(g10,g1)
    c: Tangent(g36,g22) = 1.5708
    c: Vertical(g10)
    c: Vertical(g12)
    c: Horizontal(g22)
    c: Tangent(g34,g13) = 1.5708
    c: Coincident(g13,g2)
    c: Equal(g31,g14)
    c: Equal(g22,g33)
    c: Equal(g11,g16)
    c: Equal(g18,g20)
    c: Equal(g21,g19)
    c: Radius(g38) = 1.2
    c: Equal(g9,g17)
    c: PointOnObject(g9,g-7)
    c: Equal(g10,g15)
    c: PointOnObject(g12,g-8)
    c: Equal(g12,g32)
    c: Equal(g30,g13)
    c: Equal(g23,g29)
    c: Equal(g24,g19)
    c: Equal(g21,g28)
    c: Equal(g23,g18)
    c: Equal(g27,g6)
    c: PointOnObject(g6,g-6)
    c: Vertical(g84)
    c: Coincident(g85,g84)
    c: Horizontal(g85)
    c: Coincident(g85,g14)
    c: Coincident(g86,g14)
    c: Horizontal(g86)
    c: Coincident(g87,g86)
    c: Vertical(g87)
    c: Equal(g86,g85)
    c: Coincident(g-9,g84)
    c: Coincident(g88,g84)
    c: Vertical(g88)
    c: Tangent(g89,g91) = 1.5708
    c: Tangent(g89,g92) = -1.5708
    c: Tangent(g90,g91) = 1.5708
    c: Tangent(g90,g92) = -1.5708
    c: Equal(g89,g90)
    c: Horizontal(g91)
    c: Tangent(g93,g95) = 1.5708
    c: Tangent(g93,g96) = -1.5708
    c: Tangent(g94,g95) = 1.5708
    c: Tangent(g94,g96) = -1.5708
    c: Equal(g93,g94)
    c: Horizontal(g95)
    c: Coincident(g97,g89)
    c: Coincident(g97,g89)
    c: Coincident(g98,g89)
    c: Coincident(g98,g93)
    c: Coincident(g99,g93)
    c: Coincident(g99,g93)
    c: Coincident(g100,g93)
    c: Vertical(g100)
    c: Equal(g97,g98)
    c: Vertical(g98)
    c: Equal(g99,g98)
    c: Equal(g100,g99)
    c: Vertical(g101)
    c: Coincident(g102,g101)
    c: Vertical(g102)
    c: Coincident(g103,g102)
    c: Vertical(g103)
    c: Coincident(g90,g87)
    c: Tangent(g104,g106) = 1.5708
    c: Tangent(g104,g107) = -1.5708
    c: Tangent(g105,g106) = 1.5708
    c: Tangent(g105,g107) = -1.5708
    c: Coincident(g101,g104)
    c: Coincident(g100,g101)
    c: Coincident(g100,g104)
    c: Horizontal(g106)
    c: Tangent(g108,g110) = 1.5708
    c: Tangent(g108,g111) = -1.5708
    c: Tangent(g109,g110) = 1.5708
    c: Tangent(g109,g111) = -1.5708
    c: Equal(g108,g109)
    c: Equal(g101,g100)
    c: Equal(g102,g101)
    c: Equal(g102,g103)
    c: Coincident(g102,g108)
    c: Coincident(g108,g103)
    c: Coincident(g112,g87)
    c: Vertical(g112)
    c: Coincident(g109,g112)
    c: PointOnObject(g105,g112)
    c: PointOnObject(g94,g112)
    c: Coincident(g88,g89)
    c: DistanceY(g88,g88) = 10
    c: DistanceY(g84,g103) = 40
    c: Distance(g31,g110) = 13.0542
    c: Distance(g14,g92) = 13.0542
FEATURE [PartDesign::Pad] Pad
  Direction = (0,0,1)
  Length = 1.8542
  Length2 = 10
  Profile = -> Sketch
  ReferenceAxis = -> Sketch [N_Axis]
  Refine = true
  Suppressed = false
  Type = 0
  expr: Length = dimensions#VarSet.EnclosureTotalThickness
FEATURE [PartDesign::Body] Body  label="PsuSideLong"
  AllowCompound = false
  Group = -> [Binder,Binder001,Sketch,Pad]
  Origin = -> Origin
  Tip = -> Pad
---- part parts/psu/psu_side_short.FCStd = doc fcstd_0afd02fb2cd9 ----
FCSTD DOCUMENT  (FreeCAD 1.0R38641 +468 (Git))
Label: psu_side_short
License: All rights reserved
LicenseURL: https://en.wikipedia.org/wiki/All_rights_reserved
objects: PartDesign::SubShapeBinder×2, Sketcher::SketchObject×1, PartDesign::Pad×1, PartDesign::Body×1
note: 8 computed .brp shape members not serialized (recipe doc carries the construction recipe); baked Part::Feature solids carry a one-line shape summary decoded from their .brp
EXTERNAL_REF file=../../third_party/qualtek_power_entry.FCStd obj=Body
EXTERNAL_REF file=psu_top_and_bottom.FCStd obj=Body
EXTERNAL_REF file=../dimensions.FCStd obj=VarSet

FEATURE [PartDesign::SubShapeBinder] Binder  label="PowerEntryBinder"
  BindCopyOnChange = 0
  BindMode = 0
  ClaimChildren = false
  Context = -> Body [Binder.]
  Fuse = false
  MakeFace = true
  OffsetFill = false
  OffsetIntersection = false
  OffsetJoinType = 0
  OffsetOpenResult = false
  PartialLoad = false
  Placement = pos=(0,0,0) rot=(1,0,0;1.5708rad)
  Refine = true
  Relative = true
  Support = -> [<external ../../third_party/qualtek_power_entry.FCStd>#Body]
  _Version = 2
FEATURE [PartDesign::SubShapeBinder] Binder001  label="PsuTopAndBottomBinder"
  BindCopyOnChange = 0
  BindMode = 0
  ClaimChildren = false
  Context = -> Body [Binder001.]
  Fuse = false
  MakeFace = true
  OffsetFill = false
  OffsetIntersection = false
  OffsetJoinType = 0
  OffsetOpenResult = false
  PartialLoad = false
  Refine = true
  Relative = true
  Support = -> [<external psu_top_and_bottom.FCStd>#Body]
  _Version = 2
FEATURE [Sketcher::SketchObject] Sketch
  ArcFitTolerance = 1e-06
  AttachmentSupport = -> [Binder001]
  ExternalGeometry = -> [Binder001,Binder]
  FullyConstrained = true
  MakeInternals = false
  MapMode = 5
  Placement = pos=(326.108,0,0) rot=(0.57735,0.57735,0.57735;2.0944rad)
  expr: Constraints[141] = dimensions#VarSet.EnclosureFinishThickness
  expr: Constraints[165] = dimensions#VarSet.EnclosureTotalThickness + 2 * dimensions#VarSet.EnclosureFinishThickness
  expr: Constraints[2] = dimensions#VarSet.EnclosureFinishThickness
  expr: Constraints[31] = dimensions#VarSet.EnclosureCornerRadius
  expr: Constraints[3] = dimensions#VarSet.EnclosureFinishThickness
  sketch-geometry (76):
    g0: LineSegment [constr] StartX=129.081 StartY=-24.706 StartZ=0 EndX=129.081 EndY=-87.794 EndZ=0
    g1: LineSegment StartX=129.081 StartY=-24.706 StartZ=0 EndX=127.227 EndY=-24.706 EndZ=0
    g2: LineSegment StartX=129.081 StartY=-87.794 StartZ=0 EndX=127.227 EndY=-87.794 EndZ=0
    g3: LineSegment StartX=126.027 StartY=-86.594 StartZ=0 EndX=126.027 EndY=-25.906 EndZ=0
    g4: ArcOfCircle CenterX=129.081 CenterY=-88.994 CenterZ=0 NormalX=0 NormalY=0 NormalZ=1 AngleXU=0 Radius=1.2 StartAngle=-2.7e-15 EndAngle=1.5708
    g5: ArcOfCircle CenterX=129.081 CenterY=-23.506 CenterZ=0 NormalX=0 NormalY=0 NormalZ=1 AngleXU=0 Radius=1.2 StartAngle=4.71239 EndAngle=6.28319
    g6: LineSegment StartX=130.281 StartY=-11.1254 StartZ=0 EndX=130.281 EndY=-23.506 EndZ=0
    g7: LineSegment StartX=130.281 StartY=-88.994 StartZ=0 EndX=130.281 EndY=-101.375 EndZ=0
    g8: LineSegment StartX=131.481 StartY=-102.575 StartZ=0 EndX=176.681 EndY=-102.575 EndZ=0
    g9: LineSegment StartX=131.481 StartY=-9.9254 StartZ=0 EndX=176.681 EndY=-9.9254 EndZ=0
    g10: LineSegment StartX=177.881 StartY=-11.1254 StartZ=0 EndX=177.881 EndY=-23.506 EndZ=0
    g11: LineSegment StartX=179.081 StartY=-24.706 StartZ=0 EndX=180.935 EndY=-24.706 EndZ=0
    g12: LineSegment StartX=182.135 StartY=-25.906 StartZ=0 EndX=182.135 EndY=-86.594 EndZ=0
    g13: LineSegment StartX=180.935 StartY=-87.794 StartZ=0 EndX=179.081 EndY=-87.794 EndZ=0
    g14: LineSegment StartX=177.881 StartY=-88.994 StartZ=0 EndX=177.881 EndY=-101.375 EndZ=0
    g15: ArcOfCircle CenterX=179.081 CenterY=-23.506 CenterZ=0 NormalX=0 NormalY=0 NormalZ=1 AngleXU=0 Radius=1.2 StartAngle=3.14159 EndAngle=4.71239
    g16: GeomPoint [constr] X=177.881 Y=-24.706 Z=0
    g17: ArcOfCircle CenterX=179.081 CenterY=-88.994 CenterZ=0 NormalX=0 NormalY=0 NormalZ=1 AngleXU=0 Radius=1.2 StartAngle=1.5708 EndAngle=3.14159
    g18: ArcOfCircle CenterX=127.227 CenterY=-25.906 CenterZ=0 NormalX=0 NormalY=0 NormalZ=1 AngleXU=0 Radius=1.2 StartAngle=1.5708 EndAngle=3.14159
    g19: GeomPoint [constr] X=126.027 Y=-24.706 Z=0
    g20: ArcOfCircle CenterX=127.227 CenterY=-86.594 CenterZ=0 NormalX=0 NormalY=0 NormalZ=1 AngleXU=0 Radius=1.2 StartAngle=3.14159 EndAngle=4.71239
    g21: GeomPoint [constr] X=126.027 Y=-87.794 Z=0
    g22: ArcOfCircle CenterX=131.481 CenterY=-101.375 CenterZ=0 NormalX=0 NormalY=0 NormalZ=1 AngleXU=0 Radius=1.2 StartAngle=3.14159 EndAngle=4.71239
    g23: GeomPoint [constr] X=130.281 Y=-102.575 Z=0
    g24: ArcOfCircle CenterX=176.681 CenterY=-101.375 CenterZ=0 NormalX=0 NormalY=0 NormalZ=1 AngleXU=0 Radius=1.2 StartAngle=4.71239 EndAngle=6.28319
    g25: GeomPoint [constr] X=177.881 Y=-102.575 Z=0
    g26: ArcOfCircle CenterX=180.935 CenterY=-86.594 CenterZ=0 NormalX=0 NormalY=0 NormalZ=1 AngleXU=0 Radius=1.2 StartAngle=4.71239 EndAngle=6.28319
    g27: GeomPoint [constr] X=182.135 Y=-87.794 Z=0
    g28: ArcOfCircle CenterX=180.935 CenterY=-25.906 CenterZ=0 NormalX=0 NormalY=0 NormalZ=1 AngleXU=0 Radius=1.2 StartAngle=0 EndAngle=1.5708
    g29: GeomPoint [constr] X=182.135 Y=-24.706 Z=0
    g30: ArcOfCircle CenterX=176.681 CenterY=-11.1254 CenterZ=0 NormalX=0 NormalY=0 NormalZ=1 AngleXU=0 Radius=1.2 StartAngle=0 EndAngle=1.5708
    g31: GeomPoint [constr] X=177.881 Y=-9.9254 Z=0
    g32: ArcOfCircle CenterX=131.481 CenterY=-11.1254 CenterZ=0 NormalX=0 NormalY=0 NormalZ=1 AngleXU=0 Radius=1.2 StartAngle=1.5708 EndAngle=3.14159
    g33: GeomPoint [constr] X=130.281 Y=-9.9254 Z=0
    g34: Circle CenterX=134.081 CenterY=-56.25 CenterZ=0 NormalX=0 NormalY=0 NormalZ=1 AngleXU=0 Radius=1.5
    g35: Circle CenterX=174.081 CenterY=-56.25 CenterZ=0 NormalX=0 NormalY=0 NormalZ=1 AngleXU=0 Radius=1.5
    g36: LineSegment [constr] StartX=140.031 StartY=-22.5 StartZ=0 EndX=140.031 EndY=-90 EndZ=0
    g37: LineSegment [constr] StartX=142.531 StartY=-92.5 StartZ=0 EndX=165.631 EndY=-92.5 EndZ=0
    g38: LineSegment [constr] StartX=168.131 StartY=-90 StartZ=0 EndX=168.131 EndY=-22.5 EndZ=0
    g39: LineSegment [constr] StartX=165.631 StartY=-20 StartZ=0 EndX=142.531 EndY=-20 EndZ=0
    g40: ArcOfCircle [constr] CenterX=142.531 CenterY=-22.5 CenterZ=0 NormalX=0 NormalY=0 NormalZ=1 AngleXU=0 Radius=2.5 StartAngle=1.5708 EndAngle=3.14159
    g41: ArcOfCircle [constr] CenterX=142.531 CenterY=-90 CenterZ=0 NormalX=0 NormalY=0 NormalZ=1 AngleXU=0 Radius=2.5 StartAngle=3.14159 EndAngle=4.71239
    g42: ArcOfCircle [constr] CenterX=165.631 CenterY=-90 CenterZ=0 NormalX=0 NormalY=0 NormalZ=1 AngleXU=0 Radius=2.5 StartAngle=4.71239 EndAngle=6.28319
    g43: ArcOfCircle [constr] CenterX=165.631 CenterY=-22.5 CenterZ=0 NormalX=0 NormalY=0 NormalZ=1 AngleXU=0 Radius=2.5 StartAngle=5e-16 EndAngle=1.5708
    g44: GeomPoint [constr] X=140.031 Y=-20 Z=0
    g45: GeomPoint [constr] X=168.131 Y=-92.5 Z=0
    g46: LineSegment [constr] StartX=126.027 StartY=-56.25 StartZ=0 EndX=134.081 EndY=-56.25 EndZ=0
    g47: LineSegment [constr] StartX=134.081 StartY=-56.25 StartZ=0 EndX=140.031 EndY=-56.25 EndZ=0
    g48: LineSegment [constr] StartX=168.131 StartY=-56.25 StartZ=0 EndX=174.081 EndY=-56.25 EndZ=0
    g49: LineSegment [constr] StartX=174.081 StartY=-56.25 StartZ=0 EndX=182.135 EndY=-56.25 EndZ=0
    g50: LineSegment [constr] StartX=-45 StartY=1.4e-14 StartZ=0 EndX=-39.05 EndY=1.31e-14 EndZ=0
    g51: LineSegment [constr] StartX=-10.95 StartY=6.1e-15 StartZ=0 EndX=-5 EndY=-1.07e-14 EndZ=0
    g52: LineSegment StartX=139.904 StartY=-22.5 StartZ=0 EndX=139.904 EndY=-90 EndZ=0
    g53: LineSegment StartX=142.531 StartY=-92.627 StartZ=0 EndX=165.631 EndY=-92.627 EndZ=0
    g54: LineSegment StartX=168.258 StartY=-90 StartZ=0 EndX=168.258 EndY=-22.5 EndZ=0
    g55: LineSegment StartX=165.631 StartY=-19.873 StartZ=0 EndX=142.531 EndY=-19.873 EndZ=0
    g56: ArcOfCircle CenterX=142.531 CenterY=-22.5 CenterZ=0 NormalX=0 NormalY=0 NormalZ=1 AngleXU=0 Radius=2.627 StartAngle=1.5708 EndAngle=3.14159
    g57: ArcOfCircle CenterX=142.531 CenterY=-90 CenterZ=0 NormalX=0 NormalY=0 NormalZ=1 AngleXU=0 Radius=2.627 StartAngle=3.14159 EndAngle=4.71239
    g58: ArcOfCircle CenterX=165.631 CenterY=-90 CenterZ=0 NormalX=0 NormalY=0 NormalZ=1 AngleXU=0 Radius=2.627 StartAngle=4.71239 EndAngle=6.28319
    g59: ArcOfCircle CenterX=165.631 CenterY=-22.5 CenterZ=0 NormalX=0 NormalY=0 NormalZ=1 AngleXU=0 Radius=2.627 StartAngle=5e-16 EndAngle=1.5708
    g60: GeomPoint [constr] X=139.904 Y=-19.873 Z=0
    g61: GeomPoint [constr] X=168.258 Y=-92.627 Z=0
    g62: LineSegment [constr] StartX=-50 StartY=7.1e-15 StartZ=0 EndX=0 EndY=0 EndZ=0
    g63: LineSegment [constr] StartX=129.081 StartY=-87.794 StartZ=0 EndX=179.081 EndY=-87.794 EndZ=0
    g64: ArcOfCircle CenterX=133.444 CenterY=-13.0877 CenterZ=0 NormalX=0 NormalY=0 NormalZ=1 AngleXU=0 Radius=1.0541 StartAngle=1.5708 EndAngle=4.71239
    g65: ArcOfCircle CenterX=174.719 CenterY=-13.0877 CenterZ=0 NormalX=0 NormalY=0 NormalZ=1 AngleXU=0 Radius=1.0541 StartAngle=4.71239 EndAngle=7.85398
    g66: LineSegment StartX=133.444 StartY=-12.0336 StartZ=0 EndX=174.719 EndY=-12.0336 EndZ=0
    g67: LineSegment StartX=133.444 StartY=-14.1418 StartZ=0 EndX=174.719 EndY=-14.1418 EndZ=0
    g68: ArcOfCircle CenterX=133.444 CenterY=-99.4123 CenterZ=0 NormalX=0 NormalY=0 NormalZ=1 AngleXU=0 Radius=1.0541 StartAngle=1.5708 EndAngle=4.71239
    g69: ArcOfCircle CenterX=174.719 CenterY=-99.4123 CenterZ=0 NormalX=0 NormalY=0 NormalZ=1 AngleXU=0 Radius=1.0541 StartAngle=4.71239 EndAngle=7.85398
    g70: LineSegment StartX=133.444 StartY=-98.3582 StartZ=0 EndX=174.719 EndY=-98.3582 EndZ=0
    g71: LineSegment StartX=133.444 StartY=-100.466 StartZ=0 EndX=174.719 EndY=-100.466 EndZ=0
    g72: LineSegment [constr] StartX=154.081 StartY=-102.575 StartZ=0 EndX=154.081 EndY=-100.466 EndZ=0
    g73: LineSegment [constr] StartX=154.081 StartY=-9.9254 StartZ=0 EndX=154.081 EndY=-12.0336 EndZ=0
    g74: LineSegment [constr] StartX=154.081 StartY=-98.3582 StartZ=0 EndX=154.081 EndY=-100.466 EndZ=0
    g75: LineSegment [constr] StartX=130.281 StartY=-99.4123 StartZ=0 EndX=132.389 EndY=-99.4123 EndZ=0
  constraints (177):
    c: PointOnObject(g0,g-3)
    c: PointOnObject(g0,g-3)
    c: DistanceY(g-3,g0) = 0.127
    c: DistanceY(g0,g-3) = 0.127
    c: Horizontal(g1)
    c: Horizontal(g2)
    c: Vertical(g3)
    c: Vertical(g6)
    c: Tangent(g5,g6) = 1.5708
    c: Vertical(g7)
    c: Tangent(g7,g4) = 1.5708
    c: Horizontal(g8)
    c: Horizontal(g9)
    c: Vertical(g10)
    c: Horizontal(g11)
    c: Vertical(g12)
    c: Horizontal(g13)
    c: Vertical(g14)
    c: PointOnObject(g16,g10)
    c: PointOnObject(g16,g11)
    c: Tangent(g10,g15) = -1.5708
    c: Tangent(g11,g15) = -1.5708
    c: Tangent(g2,g4) = -1.5708
    c: Coincident(g0,g2)
    c: Tangent(g14,g17) = -1.5708
    c: Tangent(g17,g13) = -1.5708
    c: Equal(g17,g4)
    c: Equal(g4,g5)
    c: Tangent(g1,g5) = 1.5708
    c: Coincident(g1,g0)
    c: Equal(g17,g15)
    c: Radius(g4) = 1.2
    c: PointOnObject(g19,g1)
    c: PointOnObject(g19,g3)
    c: Tangent(g1,g18) = -1.5708
    c: Tangent(g3,g18) = 1.5708
    c: PointOnObject(g21,g2)
    c: PointOnObject(g21,g3)
    c: Tangent(g2,g20) = 1.5708
    c: Tangent(g3,g20) = 1.5708
    c: PointOnObject(g23,g7)
    c: PointOnObject(g23,g8)
    c: Tangent(g7,g22) = -1.5708
    c: Tangent(g8,g22) = -1.5708
    c: PointOnObject(g25,g8)
    c: PointOnObject(g25,g14)
    c: Tangent(g8,g24) = -1.5708
    c: Tangent(g14,g24) = 1.5708
    c: PointOnObject(g27,g12)
    c: PointOnObject(g27,g13)
    c: Tangent(g12,g26) = 1.5708
    c: Tangent(g13,g26) = 1.5708
    c: PointOnObject(g29,g11)
    c: PointOnObject(g29,g12)
    c: Tangent(g11,g28) = 1.5708
    c: Tangent(g12,g28) = 1.5708
    c: PointOnObject(g31,g9)
    c: PointOnObject(g31,g10)
    c: Tangent(g9,g30) = 1.5708
    c: Tangent(g10,g30) = 1.5708
    c: PointOnObject(g33,g6)
    c: PointOnObject(g33,g9)
    c: Tangent(g6,g32) = -1.5708
    c: Tangent(g9,g32) = 1.5708
    c: PointOnObject(g-4,g9)
    c: Equal(g32,g5)
    c: Equal(g5,g18)
    c: Equal(g18,g20)
    c: Equal(g4,g22)
    c: Equal(g22,g24)
    c: Equal(g17,g26)
    c: Equal(g26,g28)
    c: Equal(g30,g15)
    c: Equal(g11,g13)
    c: Equal(g14,g10)
    c: Equal(g13,g2)
    c: Equal(g6,g10)
    c: Equal(g14,g7)
    c: PointOnObject(g2,g-5)
    c: Tangent(g36,g40) = -1.5708
    c: Tangent(g36,g41) = -1.5708
    c: Tangent(g37,g41) = -1.5708
    c: Tangent(g37,g42) = -1.5708
    c: Tangent(g38,g42) = -1.5708
    c: Tangent(g38,g43) = -1.5708
    c: Tangent(g39,g43) = -1.5708
    c: Tangent(g39,g40) = -1.5708
    c: Vertical(g36)
    c: Vertical(g38)
    c: Horizontal(g37)
    c: Horizontal(g39)
    c: Equal(g40,g41)
    c: Equal(g41,g42)
    c: Equal(g42,g43)
    c: PointOnObject(g44,g36)
    c: PointOnObject(g44,g39)
    c: PointOnObject(g45,g37)
    c: PointOnObject(g45,g38)
    c: Equal(g40,g-15)
    c: Equal(g39,g-14)
    c: Equal(g36,g-8)
    c: Symmetric(g3,g3,g46)
    c: Coincident(g46,g34)
    c: Horizontal(g46)
    c: Coincident(g47,g34)
    c: Symmetric(g36,g36,g47)
    c: Horizontal(g47)
    c: Symmetric(g38,g38,g48)
    c: Coincident(g48,g35)
    c: Horizontal(g48)
    c: Equal(g46,g49)
    c: Coincident(g50,g-7)
    c: Symmetric(g-8,g-8,g50)
    c: Symmetric(g-12,g-12,g51)
    c: Coincident(g51,g-6)
    c: Equal(g51,g48)
    c: Equal(g47,g50)
    c: Coincident(g49,g35)
    c: Symmetric(g12,g12,g49)
    c: Diameter(g34) = 3
    c: Equal(g35,g34)
    c: Tangent(g52,g56) = -1.5708
    c: Tangent(g52,g57) = -1.5708
    c: Tangent(g53,g57) = -1.5708
    c: Tangent(g53,g58) = -1.5708
    c: Tangent(g54,g58) = -1.5708
    c: Tangent(g54,g59) = -1.5708
    c: Tangent(g55,g59) = -1.5708
    c: Tangent(g55,g56) = -1.5708
    c: Vertical(g52)
    c: Vertical(g54)
    c: Horizontal(g53)
    c: Horizontal(g55)
    c: Equal(g58,g59)
    c: PointOnObject(g60,g52)
    c: PointOnObject(g60,g55)
    c: PointOnObject(g61,g53)
    c: PointOnObject(g61,g54)
    c: Coincident(g58,g42)
    c: Coincident(g57,g41)
    c: Coincident(g56,g40)
    c: Distance(g55,g39) = 0.127
    c: Coincident(g62,g-16)
    c: Coincident(g62,g-1)
    c: Coincident(g63,g0)
    c: Coincident(g63,g13)
    c: Equal(g63,g62)
    c: Tangent(g64,g66) = 1.5708
    c: Tangent(g64,g67) = -1.5708
    c: Tangent(g65,g66) = 1.5708
    c: Tangent(g65,g67) = -1.5708
    c: Equal(g64,g65)
    c: Horizontal(g66)
    c: Tangent(g68,g70) = 1.5708
    c: Tangent(g68,g71) = -1.5708
    c: Tangent(g69,g70) = 1.5708
    c: Tangent(g69,g71) = -1.5708
    c: Equal(g68,g69)
    c: Horizontal(g70)
    c: Symmetric(g8,g8,g72)
    c: Symmetric(g71,g71,g72)
    c: Vertical(g72)
    c: Symmetric(g9,g9,g73)
    c: Symmetric(g66,g66,g73)
    c: Vertical(g73)
    c: Distance(g71,g70) = 2.1082
    c: Equal(g72,g73)
    c: Symmetric(g70,g70,g74)
    c: Coincident(g74,g72)
    c: Equal(g74,g72)
    c: PointOnObject(g75,g7)
    c: PointOnObject(g75,g68)
    c: Horizontal(g75)
    c: Equal(g75,g72)
    c: Equal(g64,g68)
    c: Equal(g67,g70)
    c: Perpendicular(g68,g75)
FEATURE [PartDesign::Pad] Pad
  Direction = (1,0,0)
  Length = 1.8542
  Length2 = 10
  Profile = -> Sketch
  ReferenceAxis = -> Sketch [N_Axis]
  Refine = true
  Suppressed = false
  Type = 0
  expr: Length = dimensions#VarSet.EnclosureTotalThickness
FEATURE [PartDesign::Body] Body  label="PsuSideShort"
  AllowCompound = false
  Group = -> [Binder,Binder001,Sketch,Pad]
  Origin = -> Origin
  Tip = -> Pad
---- part parts/psu/psu_top_and_bottom.FCStd = doc fcstd_ffafd7e6628b ----
FCSTD DOCUMENT  (FreeCAD 1.0R38641 +468 (Git))
Label: psu_top_and_bottom
License: All rights reserved
LicenseURL: https://en.wikipedia.org/wiki/All_rights_reserved
objects: PartDesign::SubShapeBinder×2, Sketcher::SketchObject×1, PartDesign::Pad×1, PartDesign::Body×1
note: 8 computed .brp shape members not serialized (recipe doc carries the construction recipe); baked Part::Feature solids carry a one-line shape summary decoded from their .brp
EXTERNAL_REF file=../panel_back.FCStd obj=Body
EXTERNAL_REF file=../../third_party/doepfer_psu3.FCStd obj=Sketch
EXTERNAL_REF file=../panel_back.FCStd obj=Sketch
EXTERNAL_REF file=../../third_party/doepfer_psu3.FCStd obj=Body
EXTERNAL_REF file=../dimensions.FCStd obj=VarSet

FEATURE [PartDesign::SubShapeBinder] Binder  label="PanelBackBinder"
  BindCopyOnChange = 0
  BindMode = 0
  ClaimChildren = false
  Context = -> Body [Binder.]
  Fuse = false
  MakeFace = true
  OffsetFill = false
  OffsetIntersection = false
  OffsetJoinType = 0
  OffsetOpenResult = false
  PartialLoad = false
  Refine = true
  Relative = true
  Support = -> [<external ../panel_back.FCStd>#Body]
  _Version = 2
FEATURE [PartDesign::SubShapeBinder] Binder001  label="Psu3Binder"
  BindCopyOnChange = 0
  BindMode = 0
  ClaimChildren = false
  Context = -> Body [Binder001.]
  Fuse = false
  MakeFace = true
  OffsetFill = false
  OffsetIntersection = false
  OffsetJoinType = 0
  OffsetOpenResult = false
  PartialLoad = false
  Placement = pos=(103,130,-16.25) rot=(1,0,0;-1.5708rad)
  Refine = true
  Relative = true
  Support = -> [<external ../../third_party/doepfer_psu3.FCStd>#Body]
  _Version = 2
  expr: .Placement.Base.x = (panel_back#Sketch.Constraints.DeltaX - panel_back#Sketch.Constraints.OffsetX - doepfer_psu3#Sketch.Constraints.Width) / 2 - 10 mm
  expr: .Placement.Base.z = (doepfer_psu3#Sketch.Constraints.Height - (panel_back#Sketch.Constraints.DeltaY - panel_back#Sketch.Constraints.OffsetY)) / 2
FEATURE [Sketcher::SketchObject] Sketch
  ArcFitTolerance = 1e-06
  AttachmentSupport = -> [Binder]
  ExternalGeometry = -> [Binder001,Binder]
  FullyConstrained = true
  MakeInternals = false
  MapMode = 5
  Placement = pos=(0,127.227,-5.85e-14) rot=(0,0.707107,0.707107;3.14159rad)
  expr: Constraints[113] = dimensions#VarSet.EnclosureFinishThickness
  expr: Constraints[36] = dimensions#VarSet.EnclosureTotalThickness + 2 * dimensions#VarSet.EnclosureFinishThickness
  sketch-geometry (95):
    g0: LineSegment StartX=-330.325 StartY=-11.1254 StartZ=0 EndX=-330.325 EndY=-101.375 EndZ=0
    g1: LineSegment StartX=-96.6754 StartY=-101.375 StartZ=0 EndX=-96.6754 EndY=-11.1254 EndZ=0
    g2: Circle CenterX=-320.25 CenterY=-2.0081 CenterZ=0 NormalX=0 NormalY=0 NormalZ=1 AngleXU=0 Radius=1.627
    g3: Circle CenterX=-106.75 CenterY=-2.0081 CenterZ=0 NormalX=0 NormalY=0 NormalZ=1 AngleXU=0 Radius=1.627
    g4: Circle CenterX=-122.1 CenterY=-36.55 CenterZ=0 NormalX=0 NormalY=0 NormalZ=1 AngleXU=0 Radius=1.5
    g5: Circle CenterX=-122.1 CenterY=-75.95 CenterZ=0 NormalX=0 NormalY=0 NormalZ=1 AngleXU=0 Radius=1.5
    g6: Circle CenterX=-106.75 CenterY=-110.492 CenterZ=0 NormalX=0 NormalY=0 NormalZ=1 AngleXU=0 Radius=1.627
    g7: Circle CenterX=-320.25 CenterY=-110.492 CenterZ=0 NormalX=0 NormalY=0 NormalZ=1 AngleXU=0 Radius=1.627
    g8: Circle CenterX=-274.5 CenterY=-91.15 CenterZ=0 NormalX=0 NormalY=0 NormalZ=1 AngleXU=0 Radius=1.5
    g9: Circle CenterX=-274.5 CenterY=-21.35 CenterZ=0 NormalX=0 NormalY=0 NormalZ=1 AngleXU=0 Radius=1.5
    g10: ArcOfCircle CenterX=-329.125 CenterY=-11.1254 CenterZ=0 NormalX=0 NormalY=0 NormalZ=1 AngleXU=0 Radius=1.2 StartAngle=1.5708 EndAngle=3.14159
    g11: GeomPoint [constr] X=-330.325 Y=-9.9254 Z=0
    g12: ArcOfCircle CenterX=-329.125 CenterY=-101.375 CenterZ=0 NormalX=0 NormalY=0 NormalZ=1 AngleXU=0 Radius=1.2 StartAngle=3.14159 EndAngle=4.71239
    g13: GeomPoint [constr] X=-330.325 Y=-102.575 Z=0
    g14: ArcOfCircle CenterX=-97.8754 CenterY=-101.375 CenterZ=0 NormalX=0 NormalY=0 NormalZ=1 AngleXU=0 Radius=1.2 StartAngle=4.71239 EndAngle=6.28319
    g15: GeomPoint [constr] X=-96.6754 Y=-102.575 Z=0
    g16: ArcOfCircle CenterX=-97.8754 CenterY=-11.1254 CenterZ=0 NormalX=0 NormalY=0 NormalZ=1 AngleXU=0 Radius=1.2 StartAngle=2e-16 EndAngle=1.5708
    g17: GeomPoint [constr] X=-96.6754 Y=-9.9254 Z=0
    g18: ArcOfCircle CenterX=-327.162 CenterY=-24.579 CenterZ=0 NormalX=0 NormalY=0 NormalZ=1 AngleXU=0 Radius=1.0541 StartAngle=-9e-16 EndAngle=3.14159
    g19: ArcOfCircle CenterX=-327.162 CenterY=-87.921 CenterZ=0 NormalX=0 NormalY=0 NormalZ=1 AngleXU=0 Radius=1.0541 StartAngle=3.14159 EndAngle=6.28319
    g20: LineSegment StartX=-326.108 StartY=-24.579 StartZ=0 EndX=-326.108 EndY=-87.921 EndZ=0
    g21: LineSegment StartX=-328.216 StartY=-24.579 StartZ=0 EndX=-328.216 EndY=-87.921 EndZ=0
    g22: LineSegment [constr] StartX=-330.325 StartY=-56.25 StartZ=0 EndX=-328.216 EndY=-56.25 EndZ=0
    g23: ArcOfCircle CenterX=-99.8377 CenterY=-24.579 CenterZ=0 NormalX=0 NormalY=0 NormalZ=1 AngleXU=0 Radius=1.0541 StartAngle=-9e-16 EndAngle=3.14159
    g24: ArcOfCircle CenterX=-99.8377 CenterY=-87.921 CenterZ=0 NormalX=0 NormalY=0 NormalZ=1 AngleXU=0 Radius=1.0541 StartAngle=3.14159 EndAngle=6.28319
    g25: LineSegment StartX=-98.7836 StartY=-24.579 StartZ=0 EndX=-98.7836 EndY=-87.921 EndZ=0
    g26: LineSegment StartX=-100.892 StartY=-24.579 StartZ=0 EndX=-100.892 EndY=-87.921 EndZ=0
    g27: LineSegment [constr] StartX=-98.7836 StartY=-56.25 StartZ=0 EndX=-96.6754 EndY=-56.25 EndZ=0
    g28: ArcOfCircle CenterX=-303.647 CenterY=-13.0877 CenterZ=0 NormalX=0 NormalY=0 NormalZ=1 AngleXU=0 Radius=1.0541 StartAngle=1.5708 EndAngle=4.71239
    g29: ArcOfCircle CenterX=-240.305 CenterY=-13.0877 CenterZ=0 NormalX=0 NormalY=0 NormalZ=1 AngleXU=0 Radius=1.0541 StartAngle=4.71239 EndAngle=7.85398
    g30: LineSegment StartX=-303.647 StartY=-12.0336 StartZ=0 EndX=-240.305 EndY=-12.0336 EndZ=0
    g31: LineSegment StartX=-303.647 StartY=-14.1418 StartZ=0 EndX=-240.305 EndY=-14.1418 EndZ=0
    g32: ArcOfCircle CenterX=-186.695 CenterY=-13.0877 CenterZ=0 NormalX=0 NormalY=0 NormalZ=1 AngleXU=0 Radius=1.0541 StartAngle=1.5708 EndAngle=4.71239
    g33: ArcOfCircle CenterX=-123.353 CenterY=-13.0877 CenterZ=0 NormalX=0 NormalY=0 NormalZ=1 AngleXU=0 Radius=1.0541 StartAngle=4.71239 EndAngle=7.85398
    g34: LineSegment StartX=-186.695 StartY=-12.0336 StartZ=0 EndX=-123.353 EndY=-12.0336 EndZ=0
    g35: LineSegment StartX=-186.695 StartY=-14.1418 StartZ=0 EndX=-123.353 EndY=-14.1418 EndZ=0
    g36: ArcOfCircle CenterX=-303.647 CenterY=-99.4123 CenterZ=0 NormalX=0 NormalY=0 NormalZ=1 AngleXU=0 Radius=1.0541 StartAngle=1.5708 EndAngle=4.71239
    g37: ArcOfCircle CenterX=-240.305 CenterY=-99.4123 CenterZ=0 NormalX=0 NormalY=0 NormalZ=1 AngleXU=0 Radius=1.0541 StartAngle=4.71239 EndAngle=7.85398
    g38: LineSegment StartX=-303.647 StartY=-98.3582 StartZ=0 EndX=-240.305 EndY=-98.3582 EndZ=0
    g39: LineSegment StartX=-303.647 StartY=-100.466 StartZ=0 EndX=-240.305 EndY=-100.466 EndZ=0
    g40: ArcOfCircle CenterX=-186.695 CenterY=-99.4123 CenterZ=0 NormalX=0 NormalY=0 NormalZ=1 AngleXU=0 Radius=1.0541 StartAngle=1.5708 EndAngle=4.71239
    g41: ArcOfCircle CenterX=-123.353 CenterY=-99.4123 CenterZ=0 NormalX=0 NormalY=0 NormalZ=1 AngleXU=0 Radius=1.0541 StartAngle=4.71239 EndAngle=7.85398
    g42: LineSegment StartX=-186.695 StartY=-98.3582 StartZ=0 EndX=-123.353 EndY=-98.3582 EndZ=0
    g43: LineSegment StartX=-186.695 StartY=-100.466 StartZ=0 EndX=-123.353 EndY=-100.466 EndZ=0
    g44: LineSegment [constr] StartX=-271.976 StartY=-100.466 StartZ=0 EndX=-271.976 EndY=-102.575 EndZ=0
    g45: LineSegment [constr] StartX=-155.024 StartY=-100.466 StartZ=0 EndX=-155.024 EndY=-102.575 EndZ=0
    g46: LineSegment [constr] StartX=-155.024 StartY=-12.0336 StartZ=0 EndX=-155.024 EndY=-9.9254 EndZ=0
    g47: LineSegment [constr] StartX=-271.976 StartY=-12.0336 StartZ=0 EndX=-271.976 EndY=-9.9254 EndZ=0
    g48: LineSegment [constr] StartX=-271.976 StartY=-98.3582 StartZ=0 EndX=-271.976 EndY=-14.1418 EndZ=0
    g49: LineSegment [constr] StartX=-155.024 StartY=-14.1418 StartZ=0 EndX=-155.024 EndY=-98.3582 EndZ=0
    g50: LineSegment [constr] StartX=-257.002 StartY=2.8729 StartZ=0 EndX=-257.002 EndY=-9.9254 EndZ=0
    g51: LineSegment [constr] StartX=-257.002 StartY=-115.373 StartZ=0 EndX=-257.002 EndY=-102.575 EndZ=0
    g52: LineSegment [constr] StartX=-328.216 StartY=-56.25 StartZ=0 EndX=-326.108 EndY=-56.25 EndZ=0
    g53: LineSegment [constr] StartX=-213.5 StartY=-9.9254 StartZ=0 EndX=-213.5 EndY=-102.575 EndZ=0
    g54: LineSegment [constr] StartX=-213.627 StartY=-9.9254 StartZ=0 EndX=-213.627 EndY=-102.575 EndZ=0
    g55: LineSegment [constr] StartX=-330.325 StartY=-98.3582 StartZ=0 EndX=-271.976 EndY=-98.3582 EndZ=0
    g56: LineSegment [constr] StartX=-271.976 StartY=-98.3582 StartZ=0 EndX=-213.627 EndY=-98.3582 EndZ=0
    g57: LineSegment [constr] StartX=-155.024 StartY=-98.3582 StartZ=0 EndX=-96.6754 EndY=-98.3582 EndZ=0
    g58: LineSegment [constr] StartX=-240.305 StartY=-14.1418 StartZ=0 EndX=-240.305 EndY=-16.25 EndZ=0
    g59: LineSegment [constr] StartX=-103 StartY=-56.25 StartZ=0 EndX=-100.892 EndY=-56.25 EndZ=0
    g60: ArcOfCircle CenterX=-320.25 CenterY=-2.0081 CenterZ=0 NormalX=0 NormalY=0 NormalZ=1 AngleXU=0 Radius=3.7352 StartAngle=0 EndAngle=3.14159
    g61: LineSegment StartX=-316.515 StartY=-2.0081 StartZ=0 EndX=-316.515 EndY=-8.7254 EndZ=0
    g62: LineSegment StartX=-325.185 StartY=-9.9254 StartZ=0 EndX=-329.125 EndY=-9.9254 EndZ=0
    g63: LineSegment StartX=-329.125 StartY=-102.575 StartZ=0 EndX=-325.185 EndY=-102.575 EndZ=0
    g64: LineSegment StartX=-315.315 StartY=-102.575 StartZ=0 EndX=-111.685 EndY=-102.575 EndZ=0
    g65: LineSegment StartX=-101.815 StartY=-102.575 StartZ=0 EndX=-97.8754 EndY=-102.575 EndZ=0
    g66: LineSegment StartX=-111.685 StartY=-9.9254 StartZ=0 EndX=-315.315 EndY=-9.9254 EndZ=0
    g67: LineSegment StartX=-97.8754 StartY=-9.9254 StartZ=0 EndX=-101.815 EndY=-9.9254 EndZ=0
    g68: ArcOfCircle CenterX=-320.25 CenterY=-110.492 CenterZ=0 NormalX=0 NormalY=0 NormalZ=1 AngleXU=0 Radius=3.7352 StartAngle=3.14159 EndAngle=6.28319
    g69: ArcOfCircle CenterX=-106.75 CenterY=-110.492 CenterZ=0 NormalX=0 NormalY=0 NormalZ=1 AngleXU=0 Radius=3.7352 StartAngle=3.14159 EndAngle=6.28319
    g70: ArcOfCircle CenterX=-106.75 CenterY=-2.0081 CenterZ=0 NormalX=0 NormalY=0 NormalZ=1 AngleXU=0 Radius=3.7352 StartAngle=0 EndAngle=3.14159
    g71: LineSegment StartX=-323.985 StartY=-2.0081 StartZ=0 EndX=-323.985 EndY=-8.7254 EndZ=0
    g72: LineSegment StartX=-323.985 StartY=-110.492 StartZ=0 EndX=-323.985 EndY=-103.775 EndZ=0
    g73: LineSegment StartX=-316.515 StartY=-110.492 StartZ=0 EndX=-316.515 EndY=-103.775 EndZ=0
    g74: LineSegment StartX=-110.485 StartY=-110.492 StartZ=0 EndX=-110.485 EndY=-103.775 EndZ=0
    g75: LineSegment StartX=-103.015 StartY=-110.492 StartZ=0 EndX=-103.015 EndY=-103.775 EndZ=0
    g76: LineSegment StartX=-110.485 StartY=-2.0081 StartZ=0 EndX=-110.485 EndY=-8.7254 EndZ=0
    g77: LineSegment StartX=-103.015 StartY=-2.0081 StartZ=0 EndX=-103.015 EndY=-8.7254 EndZ=0
    g78: LineSegment [constr] StartX=-318.623 StartY=-110.492 StartZ=0 EndX=-316.515 EndY=-110.492 EndZ=0
    g79: ArcOfCircle CenterX=-325.185 CenterY=-8.7254 CenterZ=0 NormalX=0 NormalY=0 NormalZ=1 AngleXU=0 Radius=1.2 StartAngle=4.71239 EndAngle=6.28319
    g80: GeomPoint [constr] X=-323.985 Y=-9.9254 Z=0
    g81: ArcOfCircle CenterX=-315.315 CenterY=-8.7254 CenterZ=0 NormalX=0 NormalY=0 NormalZ=1 AngleXU=0 Radius=1.2 StartAngle=3.14159 EndAngle=4.71239
    g82: GeomPoint [constr] X=-316.515 Y=-9.9254 Z=0
    g83: ArcOfCircle CenterX=-111.685 CenterY=-8.7254 CenterZ=0 NormalX=0 NormalY=0 NormalZ=1 AngleXU=0 Radius=1.2 StartAngle=4.71239 EndAngle=6.28319
    g84: GeomPoint [constr] X=-110.485 Y=-9.9254 Z=0
    g85: ArcOfCircle CenterX=-101.815 CenterY=-8.7254 CenterZ=0 NormalX=0 NormalY=0 NormalZ=1 AngleXU=0 Radius=1.2 StartAngle=3.14159 EndAngle=4.71239
    g86: GeomPoint [constr] X=-103.015 Y=-9.9254 Z=0
    g87: ArcOfCircle CenterX=-111.685 CenterY=-103.775 CenterZ=0 NormalX=0 NormalY=0 NormalZ=1 AngleXU=0 Radius=1.2 StartAngle=4.8e-15 EndAngle=1.5708
    g88: GeomPoint [constr] X=-110.485 Y=-102.575 Z=0
    g89: ArcOfCircle CenterX=-101.815 CenterY=-103.775 CenterZ=0 NormalX=0 NormalY=0 NormalZ=1 AngleXU=0 Radius=1.2 StartAngle=1.5708 EndAngle=3.14159
    g90: GeomPoint [constr] X=-103.015 Y=-102.575 Z=0
    g91: ArcOfCircle CenterX=-325.185 CenterY=-103.775 CenterZ=0 NormalX=0 NormalY=0 NormalZ=1 AngleXU=0 Radius=1.2 StartAngle=3.3e-15 EndAngle=1.5708
    g92: GeomPoint [constr] X=-323.985 Y=-102.575 Z=0
    g93: ArcOfCircle CenterX=-315.315 CenterY=-103.775 CenterZ=0 NormalX=0 NormalY=0 NormalZ=1 AngleXU=0 Radius=1.2 StartAngle=1.5708 EndAngle=3.14159
    g94: GeomPoint [constr] X=-316.515 Y=-102.575 Z=0
  constraints (223):
    c: Vertical(g1)
    c: Coincident(g2,g-7)
    c: Equal(g2,g-7)
    c: Coincident(g3,g-10)
    c: Equal(g3,g-10)
    c: Coincident(g4,g-4)
    c: Equal(g4,g-4)
    c: Coincident(g5,g-5)
    c: Equal(g5,g-5)
    c: Coincident(g6,g-9)
    c: Equal(g6,g-9)
    c: Coincident(g7,g-8)
    c: Equal(g7,g-8)
    c: Coincident(g8,g-6)
    c: Equal(g8,g-6)
    c: Coincident(g9,g-3)
    c: Equal(g9,g-3)
    c: PointOnObject(g11,g0)
    c: Tangent(g0,g10) = -1.5708
    c: PointOnObject(g13,g0)
    c: Tangent(g0,g12) = -1.5708
    c: PointOnObject(g15,g1)
    c: Tangent(g1,g14) = -1.5708
    c: PointOnObject(g17,g1)
    c: Tangent(g1,g16) = -1.5708
    c: Equal(g-11,g10)
    c: Equal(g10,g12)
    c: Equal(g12,g14)
    c: Equal(g14,g16)
    c: Tangent(g18,g20) = 1.5708
    c: Tangent(g18,g21) = -1.5708
    c: Tangent(g19,g20) = 1.5708
    c: Tangent(g19,g21) = -1.5708
    c: Equal(g18,g19)
    c: Vertical(g20)
    c: Equal(g21,g-14)
    c: Distance(g20,g21) = 2.1082
    c: Symmetric(g0,g0,g22)
    c: Symmetric(g21,g21,g22)
    c: Horizontal(g22)
    c: Tangent(g23,g25) = 1.5708
    c: Tangent(g23,g26) = -1.5708
    c: Tangent(g24,g25) = 1.5708
    c: Tangent(g24,g26) = -1.5708
    c: Equal(g23,g24)
    c: Vertical(g26)
    c: Equal(g26,g21)
    c: Equal(g23,g18)
    c: Symmetric(g25,g25,g27)
    c: Symmetric(g1,g1,g27)
    c: Horizontal(g27)
    c: Equal(g27,g22)
    c: Tangent(g28,g30) = 1.5708
    c: Tangent(g28,g31) = -1.5708
    c: Tangent(g29,g30) = 1.5708
    c: Tangent(g29,g31) = -1.5708
    c: Equal(g28,g29)
    c: Horizontal(g30)
    c: Tangent(g32,g34) = 1.5708
    c: Tangent(g32,g35) = -1.5708
    c: Tangent(g33,g34) = 1.5708
    c: Tangent(g33,g35) = -1.5708
    c: Equal(g32,g33)
    c: Horizontal(g34)
    c: Equal(g29,g32)
    c: Equal(g18,g28)
    c: Tangent(g36,g38) = 1.5708
    c: Tangent(g36,g39) = -1.5708
    c: Tangent(g37,g38) = 1.5708
    c: Tangent(g37,g39) = -1.5708
    c: Equal(g36,g37)
    c: Horizontal(g38)
    c: Tangent(g40,g42) = 1.5708
    c: Tangent(g40,g43) = -1.5708
    c: Tangent(g41,g42) = 1.5708
    c: Tangent(g41,g43) = -1.5708
    c: Equal(g40,g41)
    c: Horizontal(g42)
    c: Equal(g41,g24)
    c: Equal(g40,g37)
    c: Symmetric(g39,g39,g44)
    c: Vertical(g44)
    c: Symmetric(g43,g43,g45)
    c: Vertical(g45)
    c: Symmetric(g34,g34,g46)
    c: Vertical(g46)
    c: Symmetric(g30,g30,g47)
    c: Vertical(g47)
    c: Symmetric(g38,g38,g48)
    c: Symmetric(g31,g31,g48)
    c: Vertical(g48)
    c: Equal(g44,g22)
    c: Equal(g22,g47)
    c: Equal(g47,g46)
    c: Equal(g45,g46)
    c: Symmetric(g35,g35,g49)
    c: Symmetric(g42,g42,g49)
    c: Vertical(g49)
    c: Equal(g42,g38)
    c: Equal(g38,g31)
    c: Equal(g35,g42)
    c: Equal(g31,g20)
    c: Symmetric(g-15,g-15,g50)
    c: Vertical(g50)
    c: PointOnObject(g51,g-12)
    c: Equal(g51,g50)
    c: Tangent(g51,g50)
    c: Coincident(g52,g22)
    c: Symmetric(g20,g20,g52)
    c: Equal(g52,g22)
    c: Symmetric(g67,g62,g53)
    c: Symmetric(g63,g65,g53)
    c: Vertical(g54)
    c: Distance(g53,g54) = 0.127
    c: PointOnObject(g55,g0)
    c: Horizontal(g55)
    c: Coincident(g56,g55)
    c: PointOnObject(g56,g54)
    c: Horizontal(g56)
    c: Equal(g55,g56)
    c: PointOnObject(g57,g1)
    c: Horizontal(g57)
    c: Equal(g57,g55)
    c: Coincident(g55,g48)
    c: Coincident(g57,g49)
    c: Coincident(g58,g29)
    c: PointOnObject(g58,g-16)
    c: Vertical(g58)
    c: Equal(g47,g58)
    c: Symmetric(g-17,g-17,g59)
    c: Symmetric(g26,g26,g59)
    c: Equal(g59,g27)
    c: Vertical(g0)
    c: Coincident(g60,g2)
    c: Vertical(g61)
    c: Horizontal(g62)
    c: Horizontal(g63)
    c: PointOnObject(g13,g63)
    c: PointOnObject(g15,g63)
    c: PointOnObject(g44,g63)
    c: PointOnObject(g45,g63)
    c: PointOnObject(g51,g63)
    c: PointOnObject(g54,g63)
    c: PointOnObject(g11,g67)
    c: PointOnObject(g17,g67)
    c: PointOnObject(g46,g67)
    c: PointOnObject(g47,g67)
    c: PointOnObject(g50,g67)
    c: PointOnObject(g54,g67)
    c: Coincident(g68,g7)
    c: Coincident(g69,g6)
    c: Coincident(g70,g3)
    c: Vertical(g71)
    c: Vertical(g72)
    c: Vertical(g73)
    c: Vertical(g74)
    c: Vertical(g75)
    c: Vertical(g76)
    c: Vertical(g77)
    c: Tangent(g76,g70) = -1.5708
    c: Tangent(g77,g70) = 1.5708
    c: Tangent(g61,g60) = 1.5708
    c: Tangent(g71,g60) = -1.5708
    c: Tangent(g68,g73) = -1.5708
    c: Tangent(g72,g68) = 1.5708
    c: Tangent(g69,g74) = 1.5708
    c: Tangent(g69,g75) = -1.5708
    c: Tangent(g65,g64)
    c: Tangent(g64,g63)
    c: Tangent(g62,g66)
    c: Tangent(g67,g66)
    c: Equal(g68,g60)
    c: Equal(g60,g70)
    c: Equal(g70,g69)
    c: Tangent(g12,g63) = -1.5708
    c: Tangent(g10,g62) = -1.5708
    c: Tangent(g16,g67) = -1.5708
    c: Tangent(g14,g65) = -1.5708
    c: PointOnObject(g78,g7)
    c: Coincident(g78,g68)
    c: Horizontal(g78)
    c: Equal(g78,g44)
    c: PointOnObject(g80,g62)
    c: PointOnObject(g80,g71)
    c: Tangent(g62,g79) = 1.5708
    c: Tangent(g71,g79) = 1.5708
    c: PointOnObject(g82,g61)
    c: PointOnObject(g82,g66)
    c: Tangent(g61,g81) = -1.5708
    c: Tangent(g66,g81) = 1.5708
    c: Equal(g79,g10)
    c: Equal(g79,g81)
    c: PointOnObject(g84,g66)
    c: PointOnObject(g84,g76)
    c: Tangent(g66,g83) = 1.5708
    c: Tangent(g76,g83) = 1.5708
    c: PointOnObject(g86,g67)
    c: PointOnObject(g86,g77)
    c: Tangent(g67,g85) = 1.5708
    c: Tangent(g77,g85) = -1.5708
    c: Equal(g83,g85)
    c: Equal(g85,g16)
    c: PointOnObject(g88,g64)
    c: PointOnObject(g88,g74)
    c: Tangent(g64,g87) = 1.5708
    c: Tangent(g74,g87) = -1.5708
    c: PointOnObject(g90,g65)
    c: PointOnObject(g90,g75)
    c: Tangent(g65,g89) = 1.5708
    c: Tangent(g75,g89) = 1.5708
    c: Equal(g89,g14)
    c: Equal(g87,g89)
    c: PointOnObject(g92,g63)
    c: PointOnObject(g92,g72)
    c: Tangent(g63,g91) = 1.5708
    c: Tangent(g72,g91) = -1.5708
    c: PointOnObject(g94,g64)
    c: PointOnObject(g94,g73)
    c: Tangent(g64,g93) = 1.5708
    c: Tangent(g73,g93) = 1.5708
    c: Equal(g93,g91)
    c: Equal(g91,g12)
    c: Equal(g63,g65)
FEATURE [PartDesign::Pad] Pad
  Direction = (0,1,-2e-16)
  Length = 1.8542
  Length2 = 10
  Profile = -> Sketch
  ReferenceAxis = -> Sketch [N_Axis]
  Refine = true
  Suppressed = false
  Type = 0
  expr: Length = dimensions#VarSet.EnclosureTotalThickness
FEATURE [PartDesign::Body] Body  label="PsuTopAndBottom"
  AllowCompound = false
  Group = -> [Binder,Binder001,Sketch,Pad]
  Origin = -> Origin
  Tip = -> Pad
---- part third_party/doepfer_psu3.FCStd = doc fcstd_ddf12d2bbb42 ----
FCSTD DOCUMENT  (FreeCAD 1.0R38641 +468 (Git))
Label: doepfer_psu3
License: All rights reserved
LicenseURL: https://en.wikipedia.org/wiki/All_rights_reserved
objects: Sketcher::SketchObject×1, PartDesign::Pad×1, PartDesign::Body×1
note: 6 computed .brp shape members not serialized (recipe doc carries the construction recipe); baked Part::Feature solids carry a one-line shape summary decoded from their .brp

FEATURE [Sketcher::SketchObject] Sketch
  ArcFitTolerance = 1e-06
  AttachmentSupport = -> [XY_Plane]
  FullyConstrained = true
  MakeInternals = false
  MapMode = 5
  expr: Constraints[26] = 152.4
  sketch-geometry (10):
    g0: LineSegment StartX=0 StartY=0 StartZ=0 EndX=201 EndY=0 EndZ=0
    g1: LineSegment StartX=201 StartY=0 StartZ=0 EndX=201 EndY=80 EndZ=0
    g2: LineSegment StartX=201 StartY=80 StartZ=0 EndX=0 EndY=80 EndZ=0
    g3: LineSegment StartX=0 StartY=80 StartZ=0 EndX=0 EndY=0 EndZ=0
    g4: Circle CenterX=19.1 CenterY=59.7 CenterZ=0 NormalX=0 NormalY=0 NormalZ=1 AngleXU=0 Radius=1.5
    g5: Circle CenterX=19.1 CenterY=20.3 CenterZ=0 NormalX=0 NormalY=0 NormalZ=1 AngleXU=0 Radius=1.5
    g6: Circle CenterX=171.5 CenterY=74.9 CenterZ=0 NormalX=0 NormalY=0 NormalZ=1 AngleXU=0 Radius=1.5
    g7: Circle CenterX=171.5 CenterY=5.1 CenterZ=0 NormalX=0 NormalY=0 NormalZ=1 AngleXU=0 Radius=1.5
    g8: LineSegment [constr] StartX=19.1 StartY=20.3 StartZ=0 EndX=19.1 EndY=59.7 EndZ=0
    g9: LineSegment [constr] StartX=171.5 StartY=74.9 StartZ=0 EndX=171.5 EndY=5.1 EndZ=0
  constraints (29):
    c: Coincident(g0,g1)
    c: Coincident(g1,g2)
    c: Coincident(g2,g3)
    c: Coincident(g3,g0)
    c: Horizontal(g0)
    c: Horizontal(g2)
    c: Vertical(g1)
    c: Vertical(g3)
    c: Coincident(g0,g-1)
    c: DistanceY(g3,g3) = 80  'Height'
    c: DistanceX(g0,g0) = 201  'Width'
    c: DistanceY(g7,g6) = 69.8
    c: DistanceY(g5,g4) = 39.4
    c: DistanceX(g0,g5) = 19.1
    c: Coincident(g8,g5)
    c: Coincident(g8,g4)
    c: Coincident(g9,g6)
    c: Coincident(g9,g7)
    c: Vertical(g9)
    c: Vertical(g8)
    c: Diameter(g5) = 3  'PsuHoleDiameter'
    c: DistanceY(g0,g5) = 20.3
    c: Equal(g5,g4)
    c: Equal(g5,g7)
    c: Equal(g5,g6)
    c: DistanceY(g0,g7) = 5.1
    c: DistanceX(g5,g7) = 152.4
    c: DistanceY(g0,g6) = 74.9
    c: DistanceX(g0,g7) = 171.5
FEATURE [PartDesign::Pad] Pad
  Direction = (0,0,1)
  Length = 1
  Length2 = 10
  Profile = -> Sketch
  ReferenceAxis = -> Sketch [N_Axis]
  Refine = true
  Suppressed = false
  Type = 0
FEATURE [PartDesign::Body] Body  label="Psu"
  AllowCompound = false
  Group = -> [Sketch,Pad]
  Origin = -> Origin
  Tip = -> Pad
---- part third_party/qualtek_power_entry.FCStd = doc fcstd_482ec4930a67 ----
FCSTD DOCUMENT  (FreeCAD 1.0R38641 +468 (Git))
Label: qualtek_power_entry
License: All rights reserved
LicenseURL: https://en.wikipedia.org/wiki/All_rights_reserved
objects: Sketcher::SketchObject×2, PartDesign::Pad×1, PartDesign::Pocket×1, PartDesign::Body×1
note: 11 computed .brp shape members not serialized (recipe doc carries the construction recipe); baked Part::Feature solids carry a one-line shape summary decoded from their .brp

FEATURE [Sketcher::SketchObject] Sketch001
  ArcFitTolerance = 1e-06
  FullyConstrained = false
  MakeInternals = false
  MapMode = 5
  Placement = pos=(0,0,0) rot=(0.57735,0.57735,0.57735;2.0944rad)
  sketch-geometry (17):
    g0: LineSegment StartX=39 StartY=9.70127 StartZ=0 EndX=39 EndY=40.2987 EndZ=0
    g1: LineSegment StartX=-39 StartY=40.2987 StartZ=0 EndX=-39 EndY=9.70127 EndZ=0
    g2: LineSegment StartX=36.545 StartY=43.2488 StartZ=0 EndX=0 EndY=50 EndZ=0
    g3: LineSegment StartX=0 StartY=50 StartZ=0 EndX=-36.545 EndY=43.2488 EndZ=0
    g4: LineSegment StartX=-36.545 StartY=6.75119 StartZ=0 EndX=0 EndY=0 EndZ=0
    g5: LineSegment StartX=0 StartY=0 StartZ=0 EndX=36.545 EndY=6.75119 EndZ=0
    g6: ArcOfCircle CenterX=-36 CenterY=40.2987 CenterZ=0 NormalX=0 NormalY=0 NormalZ=1 AngleXU=0 Radius=3 StartAngle=1.75347 EndAngle=3.14159
    g7: GeomPoint [constr] X=-39 Y=42.7953 Z=0
    g8: ArcOfCircle CenterX=36 CenterY=40.2987 CenterZ=0 NormalX=0 NormalY=0 NormalZ=1 AngleXU=0 Radius=3 StartAngle=7e-16 EndAngle=1.38812
    g9: GeomPoint [constr] X=39 Y=42.7953 Z=0
    g10: ArcOfCircle CenterX=36 CenterY=9.70127 CenterZ=0 NormalX=0 NormalY=0 NormalZ=1 AngleXU=0 Radius=3 StartAngle=4.89507 EndAngle=6.28319
    g11: GeomPoint [constr] X=39 Y=7.20472 Z=0
    g12: ArcOfCircle CenterX=-36 CenterY=9.70127 CenterZ=0 NormalX=0 NormalY=0 NormalZ=1 AngleXU=0 Radius=3 StartAngle=3.14159 EndAngle=4.52971
    g13: GeomPoint [constr] X=-39 Y=7.20472 Z=0
    g14: LineSegment [constr] StartX=-39 StartY=25 StartZ=0 EndX=39 EndY=25 EndZ=0
    g15: LineSegment [constr] StartX=0 StartY=50 StartZ=0 EndX=2.5e-15 EndY=25 EndZ=0
    g16: LineSegment [constr] StartX=2.5e-15 StartY=25 StartZ=0 EndX=0 EndY=0 EndZ=0
  constraints (38):
    c: Vertical(g0)
    c: Vertical(g1)
    c: Coincident(g2,g3)
    c: Coincident(g4,g5)
    c: DistanceY(g4,g2) = 50
    c: DistanceX(g13,g11) = 78
    c: PointOnObject(g7,g1)
    c: PointOnObject(g7,g3)
    c: Tangent(g1,g6) = -1.5708
    c: Tangent(g3,g6) = -1.5708
    c: PointOnObject(g9,g0)
    c: PointOnObject(g9,g2)
    c: Tangent(g0,g8) = -1.5708
    c: Tangent(g2,g8) = -1.5708
    c: PointOnObject(g11,g0)
    c: PointOnObject(g11,g5)
    c: Tangent(g0,g10) = -1.5708
    c: Tangent(g5,g10) = -1.5708
    c: PointOnObject(g13,g1)
    c: PointOnObject(g13,g4)
    c: Tangent(g1,g12) = -1.5708
    c: Tangent(g4,g12) = -1.5708
    c: Equal(g12,g6)
    c: Equal(g6,g8)
    c: Equal(g8,g10)
    c: Radius(g6) = 3
    c: Equal(g3,g2)
    c: Coincident(g4,g-1)
    c: Equal(g0,g1)
    c: Equal(g5,g4)
    c: PointOnObject(g2,g-2)
    c: Symmetric(g1,g1,g14)
    c: Symmetric(g0,g0,g14)
    c: Coincident(g15,g2)
    c: Symmetric(g14,g14,g15)
    c: Coincident(g16,g15)
    c: Coincident(g16,g4)
    c: Equal(g16,g15)
FEATURE [Sketcher::SketchObject] Sketch
  ArcFitTolerance = 1e-06
  AttachmentSupport = -> [YZ_Plane]
  ExternalGeometry = -> [Sketch001]
  FullyConstrained = true
  MakeInternals = false
  MapMode = 5
  Placement = pos=(0,0,0) rot=(0.57735,0.57735,0.57735;2.0944rad)
  sketch-geometry (18):
    g0: LineSegment StartX=-33.75 StartY=10.95 StartZ=0 EndX=33.75 EndY=10.95 EndZ=0
    g1: LineSegment StartX=36.25 StartY=13.45 StartZ=0 EndX=36.25 EndY=36.55 EndZ=0
    g2: LineSegment StartX=33.75 StartY=39.05 StartZ=0 EndX=-33.75 EndY=39.05 EndZ=0
    g3: LineSegment StartX=-36.25 StartY=36.55 StartZ=0 EndX=-36.25 EndY=13.45 EndZ=0
    g4: Circle CenterX=0 CenterY=45 CenterZ=0 NormalX=0 NormalY=0 NormalZ=1 AngleXU=0 Radius=1.75
    g5: Circle CenterX=-1.13e-14 CenterY=5 CenterZ=0 NormalX=0 NormalY=0 NormalZ=1 AngleXU=0 Radius=1.75
    g6: ArcOfCircle CenterX=-33.75 CenterY=36.55 CenterZ=0 NormalX=0 NormalY=0 NormalZ=1 AngleXU=0 Radius=2.5 StartAngle=1.5708 EndAngle=3.14159
    g7: GeomPoint [constr] X=-36.25 Y=39.05 Z=0
    g8: ArcOfCircle CenterX=-33.75 CenterY=13.45 CenterZ=0 NormalX=0 NormalY=0 NormalZ=1 AngleXU=0 Radius=2.5 StartAngle=3.14159 EndAngle=4.71239
    g9: GeomPoint [constr] X=-36.25 Y=10.95 Z=0
    g10: ArcOfCircle CenterX=33.75 CenterY=13.45 CenterZ=0 NormalX=0 NormalY=0 NormalZ=1 AngleXU=0 Radius=2.5 StartAngle=4.71239 EndAngle=6.28319
    g11: GeomPoint [constr] X=36.25 Y=10.95 Z=0
    g12: ArcOfCircle CenterX=33.75 CenterY=36.55 CenterZ=0 NormalX=0 NormalY=0 NormalZ=1 AngleXU=0 Radius=2.5 StartAngle=8e-16 EndAngle=1.5708
    g13: GeomPoint [constr] X=36.25 Y=39.05 Z=0
    g14: LineSegment [constr] StartX=0 StartY=45 StartZ=0 EndX=0 EndY=39.05 EndZ=0
    g15: LineSegment [constr] StartX=-1.13e-14 StartY=5 StartZ=0 EndX=-1.13e-14 EndY=10.95 EndZ=0
    g16: LineSegment [constr] StartX=0 StartY=50 StartZ=0 EndX=0 EndY=45 EndZ=0
    g17: LineSegment [constr] StartX=-1.13e-14 StartY=5 StartZ=0 EndX=0 EndY=0 EndZ=0
  constraints (42):
    c: Horizontal(g0)
    c: Horizontal(g2)
    c: Vertical(g1)
    c: Vertical(g3)
    c: Diameter(g4) = 3.5
    c: DistanceY(g5,g4) = 40
    c: DistanceY(g11,g13) = 28.1
    c: DistanceX(g9,g11) = 72.5
    c: PointOnObject(g7,g2)
    c: PointOnObject(g7,g3)
    c: Tangent(g2,g6) = -1.5708
    c: Tangent(g3,g6) = -1.5708
    c: PointOnObject(g9,g0)
    c: PointOnObject(g9,g3)
    c: Tangent(g0,g8) = -1.5708
    c: Tangent(g3,g8) = -1.5708
    c: PointOnObject(g11,g0)
    c: PointOnObject(g11,g1)
    c: Tangent(g0,g10) = -1.5708
    c: Tangent(g1,g10) = -1.5708
    c: PointOnObject(g13,g1)
    c: PointOnObject(g13,g2)
    c: Tangent(g1,g12) = -1.5708
    c: Tangent(g2,g12) = -1.5708
    c: Equal(g8,g6)
    c: Equal(g12,g10)
    c: Equal(g8,g10)
    c: Radius(g8) = 2.5
    c: Coincident(g14,g4)
    c: Symmetric(g2,g2,g14)
    c: Vertical(g14)
    c: Coincident(g15,g5)
    c: Symmetric(g0,g0,g15)
    c: Vertical(g15)
    c: Equal(g15,g14)
    c: Equal(g5,g4)
    c: Coincident(g16,g-3)
    c: Coincident(g16,g4)
    c: Vertical(g16)
    c: Coincident(g17,g5)
    c: Coincident(g17,g-1)
    c: Equal(g17,g16)
FEATURE [PartDesign::Pad] Pad
  Direction = (1,0,0)
  Length = 5
  Length2 = 10
  Placement = pos=(0,0,0) rot=(0.57735,0.57735,0.57735;2.0944rad)
  Profile = -> Sketch001
  ReferenceAxis = -> Sketch001 [N_Axis]
  Refine = true
  Suppressed = false
  Type = 0
FEATURE [PartDesign::Pocket] Pocket
  BaseFeature = -> Pad
  Direction = (-1,0,0)
  Length = 0
  Length2 = 5
  Placement = pos=(0,0,0) rot=(0.57735,0.57735,0.57735;2.0944rad)
  Profile = -> Sketch
  ReferenceAxis = -> Sketch [N_Axis]
  Refine = true
  Suppressed = false
  Type = 3
  UpToFace = -> Pad [Face12]
FEATURE [PartDesign::Body] Body  label="PowerEntry"
  AllowCompound = false
  Group = -> [Sketch001,Pad,Sketch,Pocket]
  Origin = -> Origin
  Tip = -> Pocket
